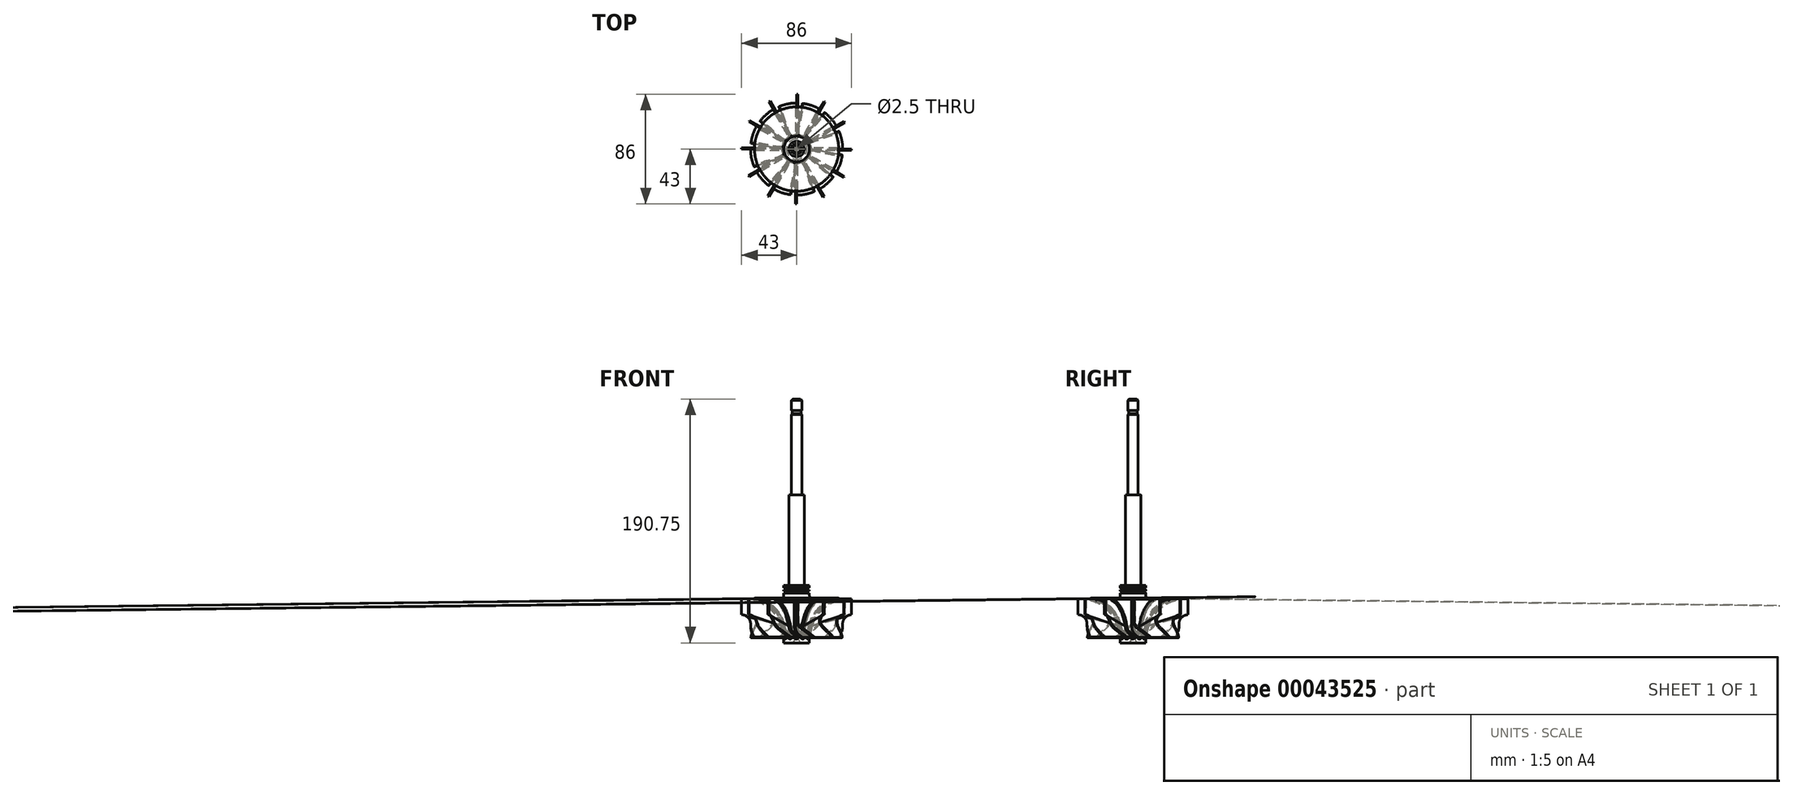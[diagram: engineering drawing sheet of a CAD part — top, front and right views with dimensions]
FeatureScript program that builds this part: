
annotation { "Feature Type Name" : "Feature", "Feature Type Description" : "" }
export const myFeature = defineFeature(function(context is Context, id is Id, definition is map)
    precondition{}
    {
        {
            var Q0;
            Q0=qCreatedBy(makeId("Front.planeOp"),FACE);
            var sketch = newSketch(context, id + "F0", { "sketchPlane" : qUnion([Q0])});
            skLineSegment(sketch, "E0", {"start": v(-6, -75) * mm, "end": v(-6, -145.75) * mm});
            skLineSegment(sketch, "E1", {"start": v(-43, -155.75) * mm, "end": v(-43, -168.75) * mm, "construction": true});
            skLineSegment(sketch, "E2", {"start": v(-43, -155.75) * mm, "end": v(-32.5, -155.75) * mm, "construction": true});
            skLineSegment(sketch, "E3", {"start": v(-10, -145.75) * mm, "end": v(-6, -145.75) * mm});
            skLineSegment(sketch, "E4", {"start": v(-6, -75) * mm, "end": v(-4, -75) * mm});
            skLineSegment(sketch, "E5", {"start": v(-4, 0) * mm, "end": v(0, 0) * mm});
            skLineSegment(sketch, "E6", {"start": v(0, 0) * mm, "end": v(0, -190.75) * mm});
            skLineSegment(sketch, "E7", {"start": v(-4, 0) * mm, "end": v(-4, -9) * mm});
            skLineSegment(sketch, "E8", {"start": v(-3.4, -9) * mm, "end": v(-3.4, -11.4) * mm});
            skLineSegment(sketch, "E9", {"start": v(-3.4, -11.4) * mm, "end": v(-4, -12) * mm});
            skLineSegment(sketch, "E10", {"start": v(-4, -12) * mm, "end": v(-4, -75) * mm});
            skLineSegment(sketch, "E11", {"start": v(-4, -9) * mm, "end": v(-3.4, -9) * mm});
            skLineSegment(sketch, "E12", {"start": v(-10, -145.75) * mm, "end": v(-10, -147.75) * mm});
            skLineSegment(sketch, "E13", {"start": v(-36, -175.75) * mm, "end": v(-36, -186.75) * mm, "construction": true});
            skLineSegment(sketch, "E14", {"start": v(-43, -168.75) * mm, "end": v(-43, -168.75) * mm});
            skLineSegment(sketch, "E15", {"start": v(-36, -186.75) * mm, "end": v(-10, -186.75) * mm, "construction": true});
            skLineSegment(sketch, "E16", {"start": v(-10, -186.75) * mm, "end": v(-10, -190.75) * mm});
            skLineSegment(sketch, "E17", {"start": v(-10, -190.75) * mm, "end": v(0, -190.75) * mm});
            skPoint(sketch, "E18.visualSharp", {"position": v(-36, -168.75) * mm});
            skArc(sketch, "E18.filletArc", {"start": v(-36, -175.75) * mm, "mid": v(-38.05, -170.8) * mm, "end": v(-43, -168.75) * mm, "construction": true});
            skLineSegment(sketch, "E19", {"start": v(-32.5, -155.75) * mm, "end": v(-32.5, -156.75) * mm, "construction": true});
            skArc(sketch, "E20", {"start": v(-32.5, -155.75) * mm, "mid": v(-33, -156.25) * mm, "end": v(-32.5, -156.75) * mm});
            skArc(sketch, "E21", {"start": v(-10, -186.75) * mm, "mid": v(-16.25, -168) * mm, "end": v(-32.5, -156.75) * mm});
            skLineSegment(sketch, "E22", {"start": v(-32.5, -155.75) * mm, "end": v(-10, -155.75) * mm});
            skLineSegment(sketch, "E23", {"start": v(-2.9, -190.75) * mm, "end": v(-1.5, -188.32) * mm});
            skLineSegment(sketch, "E24", {"start": v(-1.5, -188.32) * mm, "end": v(-1.5, -186.8) * mm});
            skLineSegment(sketch, "E25", {"start": v(-1.5, -186.8) * mm, "end": v(0, -185.9) * mm});
            skLineSegment(sketch, "E26", {"start": v(-8, -147.75) * mm, "end": v(-8, -149.25) * mm});
            skLineSegment(sketch, "E27", {"start": v(-8, -147.75) * mm, "end": v(-10, -147.75) * mm});
            skLineSegment(sketch, "E28", {"start": v(-8, -149.25) * mm, "end": v(-10, -149.25) * mm});
            skLineSegment(sketch, "E29", {"start": v(-8, -150.25) * mm, "end": v(-10, -150.25) * mm});
            skLineSegment(sketch, "E30", {"start": v(-8, -151.75) * mm, "end": v(-10, -151.75) * mm});
            skPoint(sketch, "E31.orphan", {"position": v(-8, -155.75) * mm});
            skLineSegment(sketch, "E32.trimOffspring", {"start": v(-8, -150.25) * mm, "end": v(-8, -151.75) * mm});
            skLineSegment(sketch, "E33.trimOffspring", {"start": v(-10, -149.25) * mm, "end": v(-10, -150.25) * mm});
            skLineSegment(sketch, "E34.trimOffspring", {"start": v(-10, -151.75) * mm, "end": v(-10, -155.75) * mm});
            skSolve(sketch);
        }
        {
            var Q0;
            Q0=qSketchRegion(id+"F0",true);
            var Q1;
            Q1=sQuery(id+"F0.wireOp",EDGE,"E6");
            revolve(context, id + "F1", {"entities" : qUnion([Q0]), "axis" : qUnion([Q1]), "revolveType" : RevolveType.FULL});
        }
        {
            var Q0;
            Q0=makeQuery(id+"F1.opRevolve","SWEPT_EDGE",EDGE,{"disambiguationData":[OSD([sQuery(id+"F0.wireOp",EDGE,"E22"),sQuery(id+"F0.wireOp",EDGE,"E34.trimOffspring")])]});
            fillet(context, id + "F2", {"entities" : qUnion([Q0]), "radius" : 2 * mm, "tangentPropagation" : true, "allowEdgeOverflow" : false});
        }
        {
            var Q0;
            Q0=makeQuery(id+"F1.opRevolve","SWEPT_EDGE",EDGE,{"disambiguationData":[OSD([sQuery(id+"F0.wireOp",EDGE,"E5"),sQuery(id+"F0.wireOp",EDGE,"E7")])]});
            chamfer(context, id + "F3", {"entities" : qUnion([Q0]), "width" : 1 * mm, "tangentPropagation" : true});
        }
        {
            var Q0;
            Q0=qCreatedBy(makeId("Front.planeOp"),FACE);
            var sketch = newSketch(context, id + "F4", { "sketchPlane" : qUnion([Q0])});
            skLineSegment(sketch, "E35", {"start": v(0, -1.47) * mm, "end": v(0, -247.78) * mm, "construction": true});
            skLineSegment(sketch, "E36", {"start": v(0, -155.75) * mm, "end": v(0, -181.26) * mm});
            skPoint(sketch, "E37.orphan", {"position": v(0.08, -187.45) * mm});
            skLineSegment(sketch, "E38", {"start": v(3, -186.75) * mm, "end": v(1.76, -185.5) * mm});
            skPoint(sketch, "E39.visualSharp", {"position": v(0, -183.75) * mm});
            skArc(sketch, "E39.filletArc", {"start": v(0, -181.26) * mm, "mid": v(0.46, -183.56) * mm, "end": v(1.76, -185.5) * mm});
            skLineSegment(sketch, "E40.0", {"start": v(1.59, -186.75) * mm, "end": v(1.05, -186.21) * mm});
            skArc(sketch, "E40.1", {"start": v(-1, -181.26) * mm, "mid": v(-0.47, -183.94) * mm, "end": v(1.05, -186.21) * mm});
            skLineSegment(sketch, "E40.2", {"start": v(-1, -155.75) * mm, "end": v(-1, -181.26) * mm});
            skLineSegment(sketch, "E41", {"start": v(-1, -155.75) * mm, "end": v(0, -155.75) * mm});
            skLineSegment(sketch, "E42", {"start": v(3, -186.75) * mm, "end": v(1.59, -186.75) * mm});
            skSolve(sketch);
        }
        {
            var Q0;
            Q0=qCreatedBy(makeId("Front.planeOp"),FACE);
            cPlane(context, id + "F5", {"entities" : qUnion([Q0]), "cplaneType" : CPlaneType.OFFSET, "offset" : 43 * mm, "width" : 150 * mm, "height" : 150 * mm});
        }
        {
            var Q0;
            Q0=qCreatedBy(id+"F5.planeOp",FACE);
            var sketch = newSketch(context, id + "F6", { "sketchPlane" : qUnion([Q0])});
            skLineSegment(sketch, "E43", {"start": v(0, -186.75) * mm, "end": v(18, -186.75) * mm, "construction": true});
            skLineSegment(sketch, "E44", {"start": v(0, -156.25) * mm, "end": v(0, -168.75) * mm});
            skLineSegment(sketch, "E45", {"start": v(18, -186.75) * mm, "end": v(4.42, -177.24) * mm});
            skArc(sketch, "E46", {"start": v(0, -168.75) * mm, "mid": v(1.17, -173.54) * mm, "end": v(4.42, -177.24) * mm});
            skLineSegment(sketch, "E47.0", {"start": v(16.26, -186.75) * mm, "end": v(3.85, -178.06) * mm});
            skArc(sketch, "E47.1", {"start": v(-1, -168.75) * mm, "mid": v(0.28, -174) * mm, "end": v(3.85, -178.06) * mm});
            skLineSegment(sketch, "E47.2", {"start": v(-1, -156.25) * mm, "end": v(-1, -168.75) * mm});
            skLineSegment(sketch, "E48", {"start": v(18, -186.75) * mm, "end": v(16.26, -186.75) * mm});
            skPoint(sketch, "E49.orphan", {"position": v(-14.5, -155.75) * mm});
            skPoint(sketch, "E50.orphan", {"position": v(14.5, -155.75) * mm});
            skLineSegment(sketch, "E51", {"start": v(0, -156.25) * mm, "end": v(-1, -156.25) * mm});
            skPoint(sketch, "E52.orphan", {"position": v(0, -155.75) * mm});
            skSolve(sketch);
        }
        {
            var Q1;
            Q1=qSketchRegion(id+"F4",true);
            var Q2;
            Q2=qSketchRegion(id+"F6",true);
            loft(context, id + "F7", {"operationType" : NewBodyOperationType.ADD, "sheetProfilesArray" : [{ "sheetProfileEntities" : qUnion([Q1]) }, { "sheetProfileEntities" : qUnion([Q2]) }]});
        }
        {
            var Q0;
            Q0=makeQuery(id+"F7.opLoft","SWEPT_FACE",FACE,{"disambiguationData":[OSD([sQuery(id+"F4.wireOp",EDGE,"E40.0"),sQuery(id+"F4.wireOp",EDGE,"E40.1"),sQuery(id+"F4.wireOp",EDGE,"E40.2"),sQuery(id+"F6.wireOp",EDGE,"E47.0"),sQuery(id+"F6.wireOp",EDGE,"E47.1"),sQuery(id+"F6.wireOp",EDGE,"E47.2")])]});
            var Q1;
            Q1=makeQuery(id+"F7.opLoft","SWEPT_FACE",FACE,{"disambiguationData":[OSD([sQuery(id+"F4.wireOp",EDGE,"E38"),sQuery(id+"F4.wireOp",EDGE,"E40.0"),sQuery(id+"F4.wireOp",EDGE,"E42"),sQuery(id+"F6.wireOp",EDGE,"E45"),sQuery(id+"F6.wireOp",EDGE,"E47.0"),sQuery(id+"F6.wireOp",EDGE,"E48")])]});
            var Q2;
            Q2=makeQuery(id+"F7.opLoft","CAP_FACE",FACE,{"disambiguationData":[OSD([makeQuery(id+"F6.imprint","IMPRINT",FACE,{"disambiguationData":[TD([[makeQuery(id+"F6.imprint","IMPRINT",EDGE,{"derivedFrom":sQuery(id+"F6.wireOp",EDGE,"E44")}),-1.0]])]})])],"isStart":true});
            var Q3;
            Q3=makeQuery(id+"F7.opLoft","SWEPT_FACE",FACE,{"disambiguationData":[OSD([sQuery(id+"F4.wireOp",EDGE,"E38"),sQuery(id+"F4.wireOp",EDGE,"E39.filletArc"),sQuery(id+"F4.wireOp",EDGE,"E42"),sQuery(id+"F6.wireOp",EDGE,"E45"),sQuery(id+"F6.wireOp",EDGE,"E46"),sQuery(id+"F6.wireOp",EDGE,"E48")])]});
            var Q4;
            Q4=makeQuery(id+"F7.opLoft","SWEPT_FACE",FACE,{"disambiguationData":[OSD([sQuery(id+"F4.wireOp",EDGE,"E36"),sQuery(id+"F4.wireOp",EDGE,"E39.filletArc"),sQuery(id+"F4.wireOp",EDGE,"E41"),sQuery(id+"F6.wireOp",EDGE,"E44"),sQuery(id+"F6.wireOp",EDGE,"E46"),sQuery(id+"F6.wireOp",EDGE,"E51")])]});
            var Q5;
            Q5=makeQuery(id+"F7.opLoft","SWEPT_FACE",FACE,{"disambiguationData":[OSD([sQuery(id+"F4.wireOp",EDGE,"E40.1"),sQuery(id+"F4.wireOp",EDGE,"E40.2"),sQuery(id+"F4.wireOp",EDGE,"E41"),sQuery(id+"F6.wireOp",EDGE,"E47.1"),sQuery(id+"F6.wireOp",EDGE,"E47.2"),sQuery(id+"F6.wireOp",EDGE,"E51")])]});
            var Q6;
            Q6=makeQuery(id+"F7.opLoft","SWEPT_FACE",FACE,{"disambiguationData":[OSD([sQuery(id+"F4.wireOp",EDGE,"E36"),sQuery(id+"F4.wireOp",EDGE,"E40.2"),sQuery(id+"F4.wireOp",EDGE,"E41"),sQuery(id+"F6.wireOp",EDGE,"E44"),sQuery(id+"F6.wireOp",EDGE,"E47.2"),sQuery(id+"F6.wireOp",EDGE,"E51")])]});
            var Q7;
            Q7=makeQuery(id+"F1.opRevolve","SWEPT_FACE",FACE,{"disambiguationData":[OSD([sQuery(id+"F0.wireOp",EDGE,"E0")])]});
            circularPattern(context, id + "F8", {"faces" : qUnion([Q0, Q1, Q2, Q3, Q4, Q5, Q6]), "axis" : qUnion([Q7]), "angle" : 30 * degree, "instanceCount" : round(12), "patternType" : PatternType.FACE});
        }
        {
            var Q0;
            Q0=qCreatedBy(makeId("Front.planeOp"),FACE);
            var sketch = newSketch(context, id + "F9", { "sketchPlane" : qUnion([Q0])});
            skLineSegment(sketch, "E53.0", {"start": v(43, -156.25) * mm, "end": v(43, -168.75) * mm});
            skLineSegment(sketch, "E54", {"start": v(43, -168.75) * mm, "end": v(43, -168.75) * mm});
            skLineSegment(sketch, "E55", {"start": v(36, -175.75) * mm, "end": v(36, -190.75) * mm});
            skLineSegment(sketch, "E56", {"start": v(0, 28.12) * mm, "end": v(0, -228.95) * mm, "construction": true});
            skLineSegment(sketch, "E57", {"start": v(43, -168.75) * mm, "end": v(50.1, -168.75) * mm});
            skLineSegment(sketch, "E58.0", {"start": v(-10, -190.75) * mm, "end": v(10, -190.75) * mm});
            skLineSegment(sketch, "E59", {"start": v(36, -190.75) * mm, "end": v(50.1, -190.75) * mm});
            skLineSegment(sketch, "E60", {"start": v(50.1, -168.75) * mm, "end": v(50.1, -190.75) * mm});
            skPoint(sketch, "E61.visualSharp", {"position": v(36, -168.75) * mm});
            skArc(sketch, "E61.filletArc", {"start": v(43, -168.75) * mm, "mid": v(38.05, -170.8) * mm, "end": v(36, -175.75) * mm});
            skSolve(sketch);
        }
        {
            var Q0;
            Q0=qSketchRegion(id+"F9",true);
            var Q1;
            Q1=sQuery(id+"F9.wireOp",EDGE,"E56");
            revolve(context, id + "F10", {"operationType" : NewBodyOperationType.REMOVE, "entities" : qUnion([Q0]), "axis" : qUnion([Q1]), "revolveType" : RevolveType.FULL, "oppositeDirection" : true});
        }
        {
            var Q0;
            Q0=qCreatedBy(makeId("Front.planeOp"),FACE);
            var sketch = newSketch(context, id + "F11", { "sketchPlane" : qUnion([Q0])});
            skLineSegment(sketch, "E62", {"start": v(0, 44.53) * mm, "end": v(0, -214.06) * mm, "construction": true});
            skLineSegment(sketch, "E63.0", {"start": v(0, -190.75) * mm, "end": v(2.98, -190.75) * mm});
            skLineSegment(sketch, "E64", {"start": v(0, -190.75) * mm, "end": v(0, -185) * mm});
            skLineSegment(sketch, "E65", {"start": v(0, -185) * mm, "end": v(1.25, -185.75) * mm});
            skLineSegment(sketch, "E66", {"start": v(1.25, -185.75) * mm, "end": v(1.25, -187.75) * mm});
            skLineSegment(sketch, "E67", {"start": v(1.25, -187.75) * mm, "end": v(2.98, -190.75) * mm});
            skPoint(sketch, "E68.orphan", {"position": v(10, -190.75) * mm});
            skPoint(sketch, "E69.orphan", {"position": v(-10, -190.75) * mm});
            skSolve(sketch);
        }
        {
            var Q0;
            Q0=qSketchRegion(id+"F11",true);
            var Q1;
            Q1=sQuery(id+"F11.wireOp",EDGE,"E62");
            revolve(context, id + "F12", {"operationType" : NewBodyOperationType.REMOVE, "entities" : qUnion([Q0]), "axis" : qUnion([Q1]), "revolveType" : RevolveType.FULL, "oppositeDirection" : true});
        }
        {
            var Q0;
            Q0=makeQuery(id+"F8.opPattern","COPY",EDGE,{"derivedFrom":makeQuery(id+"F7.opLoft","SWEPT_EDGE",EDGE,{"disambiguationData":[OSD([sQuery(id+"F4.wireOp",EDGE,"E38"),sQuery(id+"F4.wireOp",EDGE,"E42"),sQuery(id+"F6.wireOp",EDGE,"E45"),sQuery(id+"F6.wireOp",EDGE,"E48")])]}),"instanceName":"4"});
            var Q1;
            Q1=makeQuery(id+"F8.opPattern","COPY",EDGE,{"derivedFrom":makeQuery(id+"F7.opLoft","SWEPT_EDGE",EDGE,{"disambiguationData":[OSD([sQuery(id+"F4.wireOp",EDGE,"E38"),sQuery(id+"F4.wireOp",EDGE,"E42"),sQuery(id+"F6.wireOp",EDGE,"E45"),sQuery(id+"F6.wireOp",EDGE,"E48")])]}),"instanceName":"3"});
            var Q2;
            Q2=makeQuery(id+"F8.opPattern","COPY",EDGE,{"derivedFrom":makeQuery(id+"F7.opLoft","SWEPT_EDGE",EDGE,{"disambiguationData":[OSD([sQuery(id+"F4.wireOp",EDGE,"E38"),sQuery(id+"F4.wireOp",EDGE,"E42"),sQuery(id+"F6.wireOp",EDGE,"E45"),sQuery(id+"F6.wireOp",EDGE,"E48")])]}),"instanceName":"2"});
            var Q3;
            Q3=makeQuery(id+"F8.opPattern","COPY",EDGE,{"derivedFrom":makeQuery(id+"F7.opLoft","SWEPT_EDGE",EDGE,{"disambiguationData":[OSD([sQuery(id+"F4.wireOp",EDGE,"E38"),sQuery(id+"F4.wireOp",EDGE,"E42"),sQuery(id+"F6.wireOp",EDGE,"E45"),sQuery(id+"F6.wireOp",EDGE,"E48")])]}),"instanceName":"1"});
            var Q4;
            Q4=makeQuery(id+"F7.opLoft","SWEPT_EDGE",EDGE,{"disambiguationData":[OSD([sQuery(id+"F4.wireOp",EDGE,"E38"),sQuery(id+"F4.wireOp",EDGE,"E42"),sQuery(id+"F6.wireOp",EDGE,"E45"),sQuery(id+"F6.wireOp",EDGE,"E48")])]});
            var Q5;
            Q5=makeQuery(id+"F8.opPattern","COPY",EDGE,{"derivedFrom":makeQuery(id+"F7.opLoft","SWEPT_EDGE",EDGE,{"disambiguationData":[OSD([sQuery(id+"F4.wireOp",EDGE,"E38"),sQuery(id+"F4.wireOp",EDGE,"E42"),sQuery(id+"F6.wireOp",EDGE,"E45"),sQuery(id+"F6.wireOp",EDGE,"E48")])]}),"instanceName":"11"});
            var Q6;
            Q6=makeQuery(id+"F8.opPattern","COPY",EDGE,{"derivedFrom":makeQuery(id+"F7.opLoft","SWEPT_EDGE",EDGE,{"disambiguationData":[OSD([sQuery(id+"F4.wireOp",EDGE,"E38"),sQuery(id+"F4.wireOp",EDGE,"E42"),sQuery(id+"F6.wireOp",EDGE,"E45"),sQuery(id+"F6.wireOp",EDGE,"E48")])]}),"instanceName":"10"});
            var Q7;
            Q7=makeQuery(id+"F8.opPattern","COPY",EDGE,{"derivedFrom":makeQuery(id+"F7.opLoft","SWEPT_EDGE",EDGE,{"disambiguationData":[OSD([sQuery(id+"F4.wireOp",EDGE,"E38"),sQuery(id+"F4.wireOp",EDGE,"E42"),sQuery(id+"F6.wireOp",EDGE,"E45"),sQuery(id+"F6.wireOp",EDGE,"E48")])]}),"instanceName":"9"});
            var Q8;
            Q8=makeQuery(id+"F8.opPattern","COPY",EDGE,{"derivedFrom":makeQuery(id+"F7.opLoft","SWEPT_EDGE",EDGE,{"disambiguationData":[OSD([sQuery(id+"F4.wireOp",EDGE,"E38"),sQuery(id+"F4.wireOp",EDGE,"E42"),sQuery(id+"F6.wireOp",EDGE,"E45"),sQuery(id+"F6.wireOp",EDGE,"E48")])]}),"instanceName":"8"});
            var Q9;
            Q9=makeQuery(id+"F8.opPattern","COPY",EDGE,{"derivedFrom":makeQuery(id+"F7.opLoft","SWEPT_EDGE",EDGE,{"disambiguationData":[OSD([sQuery(id+"F4.wireOp",EDGE,"E38"),sQuery(id+"F4.wireOp",EDGE,"E42"),sQuery(id+"F6.wireOp",EDGE,"E45"),sQuery(id+"F6.wireOp",EDGE,"E48")])]}),"instanceName":"7"});
            var Q10;
            Q10=makeQuery(id+"F8.opPattern","COPY",EDGE,{"derivedFrom":makeQuery(id+"F7.opLoft","SWEPT_EDGE",EDGE,{"disambiguationData":[OSD([sQuery(id+"F4.wireOp",EDGE,"E38"),sQuery(id+"F4.wireOp",EDGE,"E42"),sQuery(id+"F6.wireOp",EDGE,"E45"),sQuery(id+"F6.wireOp",EDGE,"E48")])]}),"instanceName":"6"});
            var Q11;
            Q11=makeQuery(id+"F8.opPattern","COPY",EDGE,{"derivedFrom":makeQuery(id+"F7.opLoft","SWEPT_EDGE",EDGE,{"disambiguationData":[OSD([sQuery(id+"F4.wireOp",EDGE,"E38"),sQuery(id+"F4.wireOp",EDGE,"E42"),sQuery(id+"F6.wireOp",EDGE,"E45"),sQuery(id+"F6.wireOp",EDGE,"E48")])]}),"instanceName":"5"});
            fillet(context, id + "F13", {"entities" : qUnion([Q0, Q1, Q2, Q3, Q4, Q5, Q6, Q7, Q8, Q9, Q10, Q11]), "radius" : .3 * mm, "tangentPropagation" : true, "allowEdgeOverflow" : false});
        }
        {
            var Q0;
            Q0=makeQuery(id+"F8.opPattern","COPY",EDGE,{"derivedFrom":makeQuery(id+"F7.opLoft","SWEPT_EDGE",EDGE,{"disambiguationData":[OSD([sQuery(id+"F4.wireOp",EDGE,"E40.0"),sQuery(id+"F4.wireOp",EDGE,"E42"),sQuery(id+"F6.wireOp",EDGE,"E47.0"),sQuery(id+"F6.wireOp",EDGE,"E48")])]}),"instanceName":"5"});
            var Q1;
            Q1=makeQuery(id+"F8.opPattern","COPY",EDGE,{"derivedFrom":makeQuery(id+"F7.opLoft","SWEPT_EDGE",EDGE,{"disambiguationData":[OSD([sQuery(id+"F4.wireOp",EDGE,"E40.0"),sQuery(id+"F4.wireOp",EDGE,"E42"),sQuery(id+"F6.wireOp",EDGE,"E47.0"),sQuery(id+"F6.wireOp",EDGE,"E48")])]}),"instanceName":"4"});
            var Q2;
            Q2=makeQuery(id+"F8.opPattern","COPY",EDGE,{"derivedFrom":makeQuery(id+"F7.opLoft","SWEPT_EDGE",EDGE,{"disambiguationData":[OSD([sQuery(id+"F4.wireOp",EDGE,"E40.0"),sQuery(id+"F4.wireOp",EDGE,"E42"),sQuery(id+"F6.wireOp",EDGE,"E47.0"),sQuery(id+"F6.wireOp",EDGE,"E48")])]}),"instanceName":"3"});
            var Q3;
            Q3=makeQuery(id+"F8.opPattern","COPY",EDGE,{"derivedFrom":makeQuery(id+"F7.opLoft","SWEPT_EDGE",EDGE,{"disambiguationData":[OSD([sQuery(id+"F4.wireOp",EDGE,"E40.0"),sQuery(id+"F4.wireOp",EDGE,"E42"),sQuery(id+"F6.wireOp",EDGE,"E47.0"),sQuery(id+"F6.wireOp",EDGE,"E48")])]}),"instanceName":"2"});
            var Q4;
            Q4=makeQuery(id+"F8.opPattern","COPY",EDGE,{"derivedFrom":makeQuery(id+"F7.opLoft","SWEPT_EDGE",EDGE,{"disambiguationData":[OSD([sQuery(id+"F4.wireOp",EDGE,"E40.0"),sQuery(id+"F4.wireOp",EDGE,"E42"),sQuery(id+"F6.wireOp",EDGE,"E47.0"),sQuery(id+"F6.wireOp",EDGE,"E48")])]}),"instanceName":"1"});
            var Q5;
            Q5=makeQuery(id+"F7.opLoft","SWEPT_EDGE",EDGE,{"disambiguationData":[OSD([sQuery(id+"F4.wireOp",EDGE,"E40.0"),sQuery(id+"F4.wireOp",EDGE,"E42"),sQuery(id+"F6.wireOp",EDGE,"E47.0"),sQuery(id+"F6.wireOp",EDGE,"E48")])]});
            var Q6;
            Q6=makeQuery(id+"F8.opPattern","COPY",EDGE,{"derivedFrom":makeQuery(id+"F7.opLoft","SWEPT_EDGE",EDGE,{"disambiguationData":[OSD([sQuery(id+"F4.wireOp",EDGE,"E40.0"),sQuery(id+"F4.wireOp",EDGE,"E42"),sQuery(id+"F6.wireOp",EDGE,"E47.0"),sQuery(id+"F6.wireOp",EDGE,"E48")])]}),"instanceName":"11"});
            var Q7;
            Q7=makeQuery(id+"F8.opPattern","COPY",EDGE,{"derivedFrom":makeQuery(id+"F7.opLoft","SWEPT_EDGE",EDGE,{"disambiguationData":[OSD([sQuery(id+"F4.wireOp",EDGE,"E40.0"),sQuery(id+"F4.wireOp",EDGE,"E42"),sQuery(id+"F6.wireOp",EDGE,"E47.0"),sQuery(id+"F6.wireOp",EDGE,"E48")])]}),"instanceName":"10"});
            var Q8;
            Q8=makeQuery(id+"F8.opPattern","COPY",EDGE,{"derivedFrom":makeQuery(id+"F7.opLoft","SWEPT_EDGE",EDGE,{"disambiguationData":[OSD([sQuery(id+"F4.wireOp",EDGE,"E40.0"),sQuery(id+"F4.wireOp",EDGE,"E42"),sQuery(id+"F6.wireOp",EDGE,"E47.0"),sQuery(id+"F6.wireOp",EDGE,"E48")])]}),"instanceName":"9"});
            var Q9;
            Q9=makeQuery(id+"F8.opPattern","COPY",EDGE,{"derivedFrom":makeQuery(id+"F7.opLoft","SWEPT_EDGE",EDGE,{"disambiguationData":[OSD([sQuery(id+"F4.wireOp",EDGE,"E40.0"),sQuery(id+"F4.wireOp",EDGE,"E42"),sQuery(id+"F6.wireOp",EDGE,"E47.0"),sQuery(id+"F6.wireOp",EDGE,"E48")])]}),"instanceName":"8"});
            var Q10;
            Q10=makeQuery(id+"F8.opPattern","COPY",EDGE,{"derivedFrom":makeQuery(id+"F7.opLoft","SWEPT_EDGE",EDGE,{"disambiguationData":[OSD([sQuery(id+"F4.wireOp",EDGE,"E40.0"),sQuery(id+"F4.wireOp",EDGE,"E42"),sQuery(id+"F6.wireOp",EDGE,"E47.0"),sQuery(id+"F6.wireOp",EDGE,"E48")])]}),"instanceName":"7"});
            var Q11;
            Q11=makeQuery(id+"F8.opPattern","COPY",EDGE,{"derivedFrom":makeQuery(id+"F7.opLoft","SWEPT_EDGE",EDGE,{"disambiguationData":[OSD([sQuery(id+"F4.wireOp",EDGE,"E40.0"),sQuery(id+"F4.wireOp",EDGE,"E42"),sQuery(id+"F6.wireOp",EDGE,"E47.0"),sQuery(id+"F6.wireOp",EDGE,"E48")])]}),"instanceName":"6"});
            fillet(context, id + "F14", {"entities" : qUnion([Q0, Q1, Q2, Q3, Q4, Q5, Q6, Q7, Q8, Q9, Q10, Q11]), "radius" : 1.5 * mm, "tangentPropagation" : true, "allowEdgeOverflow" : false});
        }
        {
            var Q0;
            Q0=makeQuery(id+"F8.opPattern","COPY",EDGE,{"derivedFrom":makeQuery(id+"F7.boolean.opBoolean","INTERSECT",EDGE,{"derivedFrom":[makeQuery(id+"F1.opRevolve","SWEPT_FACE",FACE,{"disambiguationData":[OSD([sQuery(id+"F0.wireOp",EDGE,"E21")])]}),makeQuery(id+"F7.opLoft","SWEPT_FACE",FACE,{"disambiguationData":[OSD([sQuery(id+"F4.wireOp",EDGE,"E36"),sQuery(id+"F4.wireOp",EDGE,"E39.filletArc"),sQuery(id+"F4.wireOp",EDGE,"E41"),sQuery(id+"F6.wireOp",EDGE,"E44"),sQuery(id+"F6.wireOp",EDGE,"E46"),sQuery(id+"F6.wireOp",EDGE,"E51")])]})]}),"instanceName":"5"});
            var Q1;
            Q1=makeQuery(id+"F8.opPattern","COPY",EDGE,{"derivedFrom":makeQuery(id+"F7.boolean.opBoolean","INTERSECT",EDGE,{"derivedFrom":[makeQuery(id+"F1.opRevolve","SWEPT_FACE",FACE,{"disambiguationData":[OSD([sQuery(id+"F0.wireOp",EDGE,"E21")])]}),makeQuery(id+"F7.opLoft","SWEPT_FACE",FACE,{"disambiguationData":[OSD([sQuery(id+"F4.wireOp",EDGE,"E38"),sQuery(id+"F4.wireOp",EDGE,"E39.filletArc"),sQuery(id+"F4.wireOp",EDGE,"E42"),sQuery(id+"F6.wireOp",EDGE,"E45"),sQuery(id+"F6.wireOp",EDGE,"E46"),sQuery(id+"F6.wireOp",EDGE,"E48")])]})]}),"instanceName":"5"});
            var Q2;
            Q2=makeQuery(id+"F13.opFillet","BLEND_EDGE",EDGE,{"blendedFrom":[makeQuery(id+"F8.opPattern","COPY",EDGE,{"derivedFrom":makeQuery(id+"F7.opLoft","SWEPT_EDGE",EDGE,{"disambiguationData":[OSD([sQuery(id+"F4.wireOp",EDGE,"E38"),sQuery(id+"F4.wireOp",EDGE,"E42"),sQuery(id+"F6.wireOp",EDGE,"E45"),sQuery(id+"F6.wireOp",EDGE,"E48")])]}),"instanceName":"5"}),makeQuery(id+"F8.opPattern","SPLIT",FACE,{"disambiguationData":[OD(6.0)],"derivedFrom":makeQuery(id+"F1.opRevolve","SWEPT_FACE",FACE,{"disambiguationData":[OSD([sQuery(id+"F0.wireOp",EDGE,"E21")])]})})],"blendedInto":[makeQuery(id+"F8.opPattern","SPLIT",FACE,{"disambiguationData":[OD(6.0)],"derivedFrom":makeQuery(id+"F1.opRevolve","SWEPT_FACE",FACE,{"disambiguationData":[OSD([sQuery(id+"F0.wireOp",EDGE,"E21")])]})})]});
            var Q3;
            Q3=makeQuery(id+"F8.opPattern","COPY",EDGE,{"derivedFrom":makeQuery(id+"F7.boolean.opBoolean","SPLIT",EDGE,{"disambiguationData":[OD(1.0)],"derivedFrom":makeQuery(id+"F1.opRevolve","SWEPT_EDGE",EDGE,{"disambiguationData":[OSD([sQuery(id+"F0.wireOp",EDGE,"E16"),sQuery(id+"F0.wireOp",EDGE,"E21")])]})}),"instanceName":"5"});
            var Q4;
            Q4=makeQuery(id+"F14.opFillet","BLEND_EDGE",EDGE,{"blendedFrom":[makeQuery(id+"F8.opPattern","COPY",EDGE,{"derivedFrom":makeQuery(id+"F7.opLoft","SWEPT_EDGE",EDGE,{"disambiguationData":[OSD([sQuery(id+"F4.wireOp",EDGE,"E40.0"),sQuery(id+"F4.wireOp",EDGE,"E42"),sQuery(id+"F6.wireOp",EDGE,"E47.0"),sQuery(id+"F6.wireOp",EDGE,"E48")])]}),"instanceName":"5"}),makeQuery(id+"F8.opPattern","SPLIT",FACE,{"disambiguationData":[OD(5.0)],"derivedFrom":makeQuery(id+"F1.opRevolve","SWEPT_FACE",FACE,{"disambiguationData":[OSD([sQuery(id+"F0.wireOp",EDGE,"E21")])]})})],"blendedInto":[makeQuery(id+"F8.opPattern","SPLIT",FACE,{"disambiguationData":[OD(5.0)],"derivedFrom":makeQuery(id+"F1.opRevolve","SWEPT_FACE",FACE,{"disambiguationData":[OSD([sQuery(id+"F0.wireOp",EDGE,"E21")])]})})]});
            var Q5;
            Q5=makeQuery(id+"F8.opPattern","COPY",EDGE,{"derivedFrom":makeQuery(id+"F7.boolean.opBoolean","INTERSECT",EDGE,{"derivedFrom":[makeQuery(id+"F1.opRevolve","SWEPT_FACE",FACE,{"disambiguationData":[OSD([sQuery(id+"F0.wireOp",EDGE,"E21")])]}),makeQuery(id+"F7.opLoft","SWEPT_FACE",FACE,{"disambiguationData":[OSD([sQuery(id+"F4.wireOp",EDGE,"E40.0"),sQuery(id+"F4.wireOp",EDGE,"E40.1"),sQuery(id+"F4.wireOp",EDGE,"E40.2"),sQuery(id+"F6.wireOp",EDGE,"E47.0"),sQuery(id+"F6.wireOp",EDGE,"E47.1"),sQuery(id+"F6.wireOp",EDGE,"E47.2")])]})]}),"instanceName":"5"});
            var Q6;
            Q6=makeQuery(id+"F8.opPattern","COPY",EDGE,{"derivedFrom":makeQuery(id+"F7.boolean.opBoolean","INTERSECT",EDGE,{"derivedFrom":[makeQuery(id+"F1.opRevolve","SWEPT_FACE",FACE,{"disambiguationData":[OSD([sQuery(id+"F0.wireOp",EDGE,"E21")])]}),makeQuery(id+"F7.opLoft","SWEPT_FACE",FACE,{"disambiguationData":[OSD([sQuery(id+"F4.wireOp",EDGE,"E40.1"),sQuery(id+"F4.wireOp",EDGE,"E40.2"),sQuery(id+"F4.wireOp",EDGE,"E41"),sQuery(id+"F6.wireOp",EDGE,"E47.1"),sQuery(id+"F6.wireOp",EDGE,"E47.2"),sQuery(id+"F6.wireOp",EDGE,"E51")])]})]}),"instanceName":"5"});
            var Q7;
            Q7=makeQuery(id+"F8.opPattern","COPY",EDGE,{"derivedFrom":makeQuery(id+"F7.boolean.opBoolean","INTERSECT",EDGE,{"derivedFrom":[makeQuery(id+"F1.opRevolve","SWEPT_FACE",FACE,{"disambiguationData":[OSD([sQuery(id+"F0.wireOp",EDGE,"E20")])]}),makeQuery(id+"F7.opLoft","SWEPT_FACE",FACE,{"disambiguationData":[OSD([sQuery(id+"F4.wireOp",EDGE,"E40.1"),sQuery(id+"F4.wireOp",EDGE,"E40.2"),sQuery(id+"F4.wireOp",EDGE,"E41"),sQuery(id+"F6.wireOp",EDGE,"E47.1"),sQuery(id+"F6.wireOp",EDGE,"E47.2"),sQuery(id+"F6.wireOp",EDGE,"E51")])]})]}),"instanceName":"5"});
            var Q8;
            Q8=makeQuery(id+"F8.opPattern","COPY",EDGE,{"derivedFrom":makeQuery(id+"F7.boolean.opBoolean","INTERSECT",EDGE,{"derivedFrom":[makeQuery(id+"F1.opRevolve","SWEPT_FACE",FACE,{"disambiguationData":[OSD([sQuery(id+"F0.wireOp",EDGE,"E20")])]}),makeQuery(id+"F7.opLoft","SWEPT_FACE",FACE,{"disambiguationData":[OSD([sQuery(id+"F4.wireOp",EDGE,"E36"),sQuery(id+"F4.wireOp",EDGE,"E39.filletArc"),sQuery(id+"F4.wireOp",EDGE,"E41"),sQuery(id+"F6.wireOp",EDGE,"E44"),sQuery(id+"F6.wireOp",EDGE,"E46"),sQuery(id+"F6.wireOp",EDGE,"E51")])]})]}),"instanceName":"5"});
            var Q9;
            Q9=makeQuery(id+"F8.opPattern","COPY",EDGE,{"derivedFrom":makeQuery(id+"F7.boolean.opBoolean","INTERSECT",EDGE,{"derivedFrom":[makeQuery(id+"F1.opRevolve","SWEPT_FACE",FACE,{"disambiguationData":[OSD([sQuery(id+"F0.wireOp",EDGE,"E20")])]}),makeQuery(id+"F7.opLoft","SWEPT_FACE",FACE,{"disambiguationData":[OSD([sQuery(id+"F4.wireOp",EDGE,"E36"),sQuery(id+"F4.wireOp",EDGE,"E40.2"),sQuery(id+"F4.wireOp",EDGE,"E41"),sQuery(id+"F6.wireOp",EDGE,"E44"),sQuery(id+"F6.wireOp",EDGE,"E47.2"),sQuery(id+"F6.wireOp",EDGE,"E51")])]})]}),"instanceName":"5"});
            var Q10;
            Q10=makeQuery(id+"F8.opPattern","COPY",EDGE,{"derivedFrom":makeQuery(id+"F7.boolean.opBoolean","INTERSECT",EDGE,{"derivedFrom":[makeQuery(id+"F1.opRevolve","SWEPT_FACE",FACE,{"disambiguationData":[OSD([sQuery(id+"F0.wireOp",EDGE,"E21")])]}),makeQuery(id+"F7.opLoft","SWEPT_FACE",FACE,{"disambiguationData":[OSD([sQuery(id+"F4.wireOp",EDGE,"E36"),sQuery(id+"F4.wireOp",EDGE,"E39.filletArc"),sQuery(id+"F4.wireOp",EDGE,"E41"),sQuery(id+"F6.wireOp",EDGE,"E44"),sQuery(id+"F6.wireOp",EDGE,"E46"),sQuery(id+"F6.wireOp",EDGE,"E51")])]})]}),"instanceName":"6"});
            var Q11;
            Q11=makeQuery(id+"F8.opPattern","COPY",EDGE,{"derivedFrom":makeQuery(id+"F7.boolean.opBoolean","INTERSECT",EDGE,{"derivedFrom":[makeQuery(id+"F1.opRevolve","SWEPT_FACE",FACE,{"disambiguationData":[OSD([sQuery(id+"F0.wireOp",EDGE,"E21")])]}),makeQuery(id+"F7.opLoft","SWEPT_FACE",FACE,{"disambiguationData":[OSD([sQuery(id+"F4.wireOp",EDGE,"E38"),sQuery(id+"F4.wireOp",EDGE,"E39.filletArc"),sQuery(id+"F4.wireOp",EDGE,"E42"),sQuery(id+"F6.wireOp",EDGE,"E45"),sQuery(id+"F6.wireOp",EDGE,"E46"),sQuery(id+"F6.wireOp",EDGE,"E48")])]})]}),"instanceName":"6"});
            var Q12;
            Q12=makeQuery(id+"F13.opFillet","BLEND_EDGE",EDGE,{"blendedFrom":[makeQuery(id+"F8.opPattern","COPY",EDGE,{"derivedFrom":makeQuery(id+"F7.opLoft","SWEPT_EDGE",EDGE,{"disambiguationData":[OSD([sQuery(id+"F4.wireOp",EDGE,"E38"),sQuery(id+"F4.wireOp",EDGE,"E42"),sQuery(id+"F6.wireOp",EDGE,"E45"),sQuery(id+"F6.wireOp",EDGE,"E48")])]}),"instanceName":"6"}),makeQuery(id+"F8.opPattern","SPLIT",FACE,{"disambiguationData":[OD(7.0)],"derivedFrom":makeQuery(id+"F1.opRevolve","SWEPT_FACE",FACE,{"disambiguationData":[OSD([sQuery(id+"F0.wireOp",EDGE,"E21")])]})})],"blendedInto":[makeQuery(id+"F8.opPattern","SPLIT",FACE,{"disambiguationData":[OD(7.0)],"derivedFrom":makeQuery(id+"F1.opRevolve","SWEPT_FACE",FACE,{"disambiguationData":[OSD([sQuery(id+"F0.wireOp",EDGE,"E21")])]})})]});
            var Q13;
            Q13=makeQuery(id+"F8.opPattern","COPY",EDGE,{"derivedFrom":makeQuery(id+"F7.boolean.opBoolean","SPLIT",EDGE,{"disambiguationData":[OD(1.0)],"derivedFrom":makeQuery(id+"F1.opRevolve","SWEPT_EDGE",EDGE,{"disambiguationData":[OSD([sQuery(id+"F0.wireOp",EDGE,"E16"),sQuery(id+"F0.wireOp",EDGE,"E21")])]})}),"instanceName":"6"});
            var Q14;
            Q14=makeQuery(id+"F14.opFillet","BLEND_EDGE",EDGE,{"blendedFrom":[makeQuery(id+"F8.opPattern","COPY",EDGE,{"derivedFrom":makeQuery(id+"F7.opLoft","SWEPT_EDGE",EDGE,{"disambiguationData":[OSD([sQuery(id+"F4.wireOp",EDGE,"E40.0"),sQuery(id+"F4.wireOp",EDGE,"E42"),sQuery(id+"F6.wireOp",EDGE,"E47.0"),sQuery(id+"F6.wireOp",EDGE,"E48")])]}),"instanceName":"6"}),makeQuery(id+"F8.opPattern","SPLIT",FACE,{"disambiguationData":[OD(6.0)],"derivedFrom":makeQuery(id+"F1.opRevolve","SWEPT_FACE",FACE,{"disambiguationData":[OSD([sQuery(id+"F0.wireOp",EDGE,"E21")])]})})],"blendedInto":[makeQuery(id+"F8.opPattern","SPLIT",FACE,{"disambiguationData":[OD(6.0)],"derivedFrom":makeQuery(id+"F1.opRevolve","SWEPT_FACE",FACE,{"disambiguationData":[OSD([sQuery(id+"F0.wireOp",EDGE,"E21")])]})})]});
            var Q15;
            Q15=makeQuery(id+"F8.opPattern","COPY",EDGE,{"derivedFrom":makeQuery(id+"F7.boolean.opBoolean","INTERSECT",EDGE,{"derivedFrom":[makeQuery(id+"F1.opRevolve","SWEPT_FACE",FACE,{"disambiguationData":[OSD([sQuery(id+"F0.wireOp",EDGE,"E21")])]}),makeQuery(id+"F7.opLoft","SWEPT_FACE",FACE,{"disambiguationData":[OSD([sQuery(id+"F4.wireOp",EDGE,"E40.0"),sQuery(id+"F4.wireOp",EDGE,"E40.1"),sQuery(id+"F4.wireOp",EDGE,"E40.2"),sQuery(id+"F6.wireOp",EDGE,"E47.0"),sQuery(id+"F6.wireOp",EDGE,"E47.1"),sQuery(id+"F6.wireOp",EDGE,"E47.2")])]})]}),"instanceName":"6"});
            var Q16;
            Q16=makeQuery(id+"F8.opPattern","COPY",EDGE,{"derivedFrom":makeQuery(id+"F7.boolean.opBoolean","INTERSECT",EDGE,{"derivedFrom":[makeQuery(id+"F1.opRevolve","SWEPT_FACE",FACE,{"disambiguationData":[OSD([sQuery(id+"F0.wireOp",EDGE,"E21")])]}),makeQuery(id+"F7.opLoft","SWEPT_FACE",FACE,{"disambiguationData":[OSD([sQuery(id+"F4.wireOp",EDGE,"E40.1"),sQuery(id+"F4.wireOp",EDGE,"E40.2"),sQuery(id+"F4.wireOp",EDGE,"E41"),sQuery(id+"F6.wireOp",EDGE,"E47.1"),sQuery(id+"F6.wireOp",EDGE,"E47.2"),sQuery(id+"F6.wireOp",EDGE,"E51")])]})]}),"instanceName":"6"});
            var Q17;
            Q17=makeQuery(id+"F8.opPattern","COPY",EDGE,{"derivedFrom":makeQuery(id+"F7.boolean.opBoolean","INTERSECT",EDGE,{"derivedFrom":[makeQuery(id+"F1.opRevolve","SWEPT_FACE",FACE,{"disambiguationData":[OSD([sQuery(id+"F0.wireOp",EDGE,"E20")])]}),makeQuery(id+"F7.opLoft","SWEPT_FACE",FACE,{"disambiguationData":[OSD([sQuery(id+"F4.wireOp",EDGE,"E40.1"),sQuery(id+"F4.wireOp",EDGE,"E40.2"),sQuery(id+"F4.wireOp",EDGE,"E41"),sQuery(id+"F6.wireOp",EDGE,"E47.1"),sQuery(id+"F6.wireOp",EDGE,"E47.2"),sQuery(id+"F6.wireOp",EDGE,"E51")])]})]}),"instanceName":"6"});
            var Q18;
            Q18=makeQuery(id+"F8.opPattern","COPY",EDGE,{"derivedFrom":makeQuery(id+"F7.boolean.opBoolean","INTERSECT",EDGE,{"derivedFrom":[makeQuery(id+"F1.opRevolve","SWEPT_FACE",FACE,{"disambiguationData":[OSD([sQuery(id+"F0.wireOp",EDGE,"E20")])]}),makeQuery(id+"F7.opLoft","SWEPT_FACE",FACE,{"disambiguationData":[OSD([sQuery(id+"F4.wireOp",EDGE,"E36"),sQuery(id+"F4.wireOp",EDGE,"E39.filletArc"),sQuery(id+"F4.wireOp",EDGE,"E41"),sQuery(id+"F6.wireOp",EDGE,"E44"),sQuery(id+"F6.wireOp",EDGE,"E46"),sQuery(id+"F6.wireOp",EDGE,"E51")])]})]}),"instanceName":"6"});
            var Q19;
            Q19=makeQuery(id+"F8.opPattern","COPY",EDGE,{"derivedFrom":makeQuery(id+"F7.boolean.opBoolean","INTERSECT",EDGE,{"derivedFrom":[makeQuery(id+"F1.opRevolve","SWEPT_FACE",FACE,{"disambiguationData":[OSD([sQuery(id+"F0.wireOp",EDGE,"E20")])]}),makeQuery(id+"F7.opLoft","SWEPT_FACE",FACE,{"disambiguationData":[OSD([sQuery(id+"F4.wireOp",EDGE,"E36"),sQuery(id+"F4.wireOp",EDGE,"E40.2"),sQuery(id+"F4.wireOp",EDGE,"E41"),sQuery(id+"F6.wireOp",EDGE,"E44"),sQuery(id+"F6.wireOp",EDGE,"E47.2"),sQuery(id+"F6.wireOp",EDGE,"E51")])]})]}),"instanceName":"6"});
            var Q20;
            Q20=makeQuery(id+"F8.opPattern","COPY",EDGE,{"derivedFrom":makeQuery(id+"F7.boolean.opBoolean","INTERSECT",EDGE,{"derivedFrom":[makeQuery(id+"F1.opRevolve","SWEPT_FACE",FACE,{"disambiguationData":[OSD([sQuery(id+"F0.wireOp",EDGE,"E21")])]}),makeQuery(id+"F7.opLoft","SWEPT_FACE",FACE,{"disambiguationData":[OSD([sQuery(id+"F4.wireOp",EDGE,"E36"),sQuery(id+"F4.wireOp",EDGE,"E39.filletArc"),sQuery(id+"F4.wireOp",EDGE,"E41"),sQuery(id+"F6.wireOp",EDGE,"E44"),sQuery(id+"F6.wireOp",EDGE,"E46"),sQuery(id+"F6.wireOp",EDGE,"E51")])]})]}),"instanceName":"7"});
            var Q21;
            Q21=makeQuery(id+"F8.opPattern","COPY",EDGE,{"derivedFrom":makeQuery(id+"F7.boolean.opBoolean","INTERSECT",EDGE,{"derivedFrom":[makeQuery(id+"F1.opRevolve","SWEPT_FACE",FACE,{"disambiguationData":[OSD([sQuery(id+"F0.wireOp",EDGE,"E21")])]}),makeQuery(id+"F7.opLoft","SWEPT_FACE",FACE,{"disambiguationData":[OSD([sQuery(id+"F4.wireOp",EDGE,"E38"),sQuery(id+"F4.wireOp",EDGE,"E39.filletArc"),sQuery(id+"F4.wireOp",EDGE,"E42"),sQuery(id+"F6.wireOp",EDGE,"E45"),sQuery(id+"F6.wireOp",EDGE,"E46"),sQuery(id+"F6.wireOp",EDGE,"E48")])]})]}),"instanceName":"7"});
            var Q22;
            Q22=makeQuery(id+"F13.opFillet","BLEND_EDGE",EDGE,{"blendedFrom":[makeQuery(id+"F8.opPattern","COPY",EDGE,{"derivedFrom":makeQuery(id+"F7.opLoft","SWEPT_EDGE",EDGE,{"disambiguationData":[OSD([sQuery(id+"F4.wireOp",EDGE,"E38"),sQuery(id+"F4.wireOp",EDGE,"E42"),sQuery(id+"F6.wireOp",EDGE,"E45"),sQuery(id+"F6.wireOp",EDGE,"E48")])]}),"instanceName":"7"}),makeQuery(id+"F8.opPattern","SPLIT",FACE,{"disambiguationData":[OD(8.0)],"derivedFrom":makeQuery(id+"F1.opRevolve","SWEPT_FACE",FACE,{"disambiguationData":[OSD([sQuery(id+"F0.wireOp",EDGE,"E21")])]})})],"blendedInto":[makeQuery(id+"F8.opPattern","SPLIT",FACE,{"disambiguationData":[OD(8.0)],"derivedFrom":makeQuery(id+"F1.opRevolve","SWEPT_FACE",FACE,{"disambiguationData":[OSD([sQuery(id+"F0.wireOp",EDGE,"E21")])]})})]});
            var Q23;
            Q23=makeQuery(id+"F8.opPattern","COPY",EDGE,{"derivedFrom":makeQuery(id+"F7.boolean.opBoolean","SPLIT",EDGE,{"disambiguationData":[OD(1.0)],"derivedFrom":makeQuery(id+"F1.opRevolve","SWEPT_EDGE",EDGE,{"disambiguationData":[OSD([sQuery(id+"F0.wireOp",EDGE,"E16"),sQuery(id+"F0.wireOp",EDGE,"E21")])]})}),"instanceName":"7"});
            var Q24;
            Q24=makeQuery(id+"F14.opFillet","BLEND_EDGE",EDGE,{"blendedFrom":[makeQuery(id+"F8.opPattern","COPY",EDGE,{"derivedFrom":makeQuery(id+"F7.opLoft","SWEPT_EDGE",EDGE,{"disambiguationData":[OSD([sQuery(id+"F4.wireOp",EDGE,"E40.0"),sQuery(id+"F4.wireOp",EDGE,"E42"),sQuery(id+"F6.wireOp",EDGE,"E47.0"),sQuery(id+"F6.wireOp",EDGE,"E48")])]}),"instanceName":"7"}),makeQuery(id+"F8.opPattern","SPLIT",FACE,{"disambiguationData":[OD(7.0)],"derivedFrom":makeQuery(id+"F1.opRevolve","SWEPT_FACE",FACE,{"disambiguationData":[OSD([sQuery(id+"F0.wireOp",EDGE,"E21")])]})})],"blendedInto":[makeQuery(id+"F8.opPattern","SPLIT",FACE,{"disambiguationData":[OD(7.0)],"derivedFrom":makeQuery(id+"F1.opRevolve","SWEPT_FACE",FACE,{"disambiguationData":[OSD([sQuery(id+"F0.wireOp",EDGE,"E21")])]})})]});
            var Q25;
            Q25=makeQuery(id+"F8.opPattern","COPY",EDGE,{"derivedFrom":makeQuery(id+"F7.boolean.opBoolean","INTERSECT",EDGE,{"derivedFrom":[makeQuery(id+"F1.opRevolve","SWEPT_FACE",FACE,{"disambiguationData":[OSD([sQuery(id+"F0.wireOp",EDGE,"E21")])]}),makeQuery(id+"F7.opLoft","SWEPT_FACE",FACE,{"disambiguationData":[OSD([sQuery(id+"F4.wireOp",EDGE,"E40.0"),sQuery(id+"F4.wireOp",EDGE,"E40.1"),sQuery(id+"F4.wireOp",EDGE,"E40.2"),sQuery(id+"F6.wireOp",EDGE,"E47.0"),sQuery(id+"F6.wireOp",EDGE,"E47.1"),sQuery(id+"F6.wireOp",EDGE,"E47.2")])]})]}),"instanceName":"7"});
            var Q26;
            Q26=makeQuery(id+"F8.opPattern","COPY",EDGE,{"derivedFrom":makeQuery(id+"F7.boolean.opBoolean","INTERSECT",EDGE,{"derivedFrom":[makeQuery(id+"F1.opRevolve","SWEPT_FACE",FACE,{"disambiguationData":[OSD([sQuery(id+"F0.wireOp",EDGE,"E21")])]}),makeQuery(id+"F7.opLoft","SWEPT_FACE",FACE,{"disambiguationData":[OSD([sQuery(id+"F4.wireOp",EDGE,"E40.1"),sQuery(id+"F4.wireOp",EDGE,"E40.2"),sQuery(id+"F4.wireOp",EDGE,"E41"),sQuery(id+"F6.wireOp",EDGE,"E47.1"),sQuery(id+"F6.wireOp",EDGE,"E47.2"),sQuery(id+"F6.wireOp",EDGE,"E51")])]})]}),"instanceName":"7"});
            var Q27;
            Q27=makeQuery(id+"F8.opPattern","COPY",EDGE,{"derivedFrom":makeQuery(id+"F7.boolean.opBoolean","INTERSECT",EDGE,{"derivedFrom":[makeQuery(id+"F1.opRevolve","SWEPT_FACE",FACE,{"disambiguationData":[OSD([sQuery(id+"F0.wireOp",EDGE,"E20")])]}),makeQuery(id+"F7.opLoft","SWEPT_FACE",FACE,{"disambiguationData":[OSD([sQuery(id+"F4.wireOp",EDGE,"E40.1"),sQuery(id+"F4.wireOp",EDGE,"E40.2"),sQuery(id+"F4.wireOp",EDGE,"E41"),sQuery(id+"F6.wireOp",EDGE,"E47.1"),sQuery(id+"F6.wireOp",EDGE,"E47.2"),sQuery(id+"F6.wireOp",EDGE,"E51")])]})]}),"instanceName":"7"});
            var Q28;
            Q28=makeQuery(id+"F8.opPattern","COPY",EDGE,{"derivedFrom":makeQuery(id+"F7.boolean.opBoolean","INTERSECT",EDGE,{"derivedFrom":[makeQuery(id+"F1.opRevolve","SWEPT_FACE",FACE,{"disambiguationData":[OSD([sQuery(id+"F0.wireOp",EDGE,"E20")])]}),makeQuery(id+"F7.opLoft","SWEPT_FACE",FACE,{"disambiguationData":[OSD([sQuery(id+"F4.wireOp",EDGE,"E36"),sQuery(id+"F4.wireOp",EDGE,"E40.2"),sQuery(id+"F4.wireOp",EDGE,"E41"),sQuery(id+"F6.wireOp",EDGE,"E44"),sQuery(id+"F6.wireOp",EDGE,"E47.2"),sQuery(id+"F6.wireOp",EDGE,"E51")])]})]}),"instanceName":"7"});
            var Q29;
            Q29=makeQuery(id+"F8.opPattern","COPY",EDGE,{"derivedFrom":makeQuery(id+"F7.boolean.opBoolean","INTERSECT",EDGE,{"derivedFrom":[makeQuery(id+"F1.opRevolve","SWEPT_FACE",FACE,{"disambiguationData":[OSD([sQuery(id+"F0.wireOp",EDGE,"E20")])]}),makeQuery(id+"F7.opLoft","SWEPT_FACE",FACE,{"disambiguationData":[OSD([sQuery(id+"F4.wireOp",EDGE,"E36"),sQuery(id+"F4.wireOp",EDGE,"E39.filletArc"),sQuery(id+"F4.wireOp",EDGE,"E41"),sQuery(id+"F6.wireOp",EDGE,"E44"),sQuery(id+"F6.wireOp",EDGE,"E46"),sQuery(id+"F6.wireOp",EDGE,"E51")])]})]}),"instanceName":"7"});
            fillet(context, id + "F15", {"entities" : qUnion([Q0, Q1, Q2, Q3, Q4, Q5, Q6, Q7, Q8, Q9, Q10, Q11, Q12, Q13, Q14, Q15, Q16, Q17, Q18, Q19, Q20, Q21, Q22, Q23, Q24, Q25, Q26, Q27, Q28, Q29]), "radius" : 1 * mm, "tangentPropagation" : true, "allowEdgeOverflow" : false});
        }
        {
            var Q0;
            Q0=makeQuery(id+"F8.opPattern","COPY",EDGE,{"derivedFrom":makeQuery(id+"F7.boolean.opBoolean","INTERSECT",EDGE,{"derivedFrom":[makeQuery(id+"F1.opRevolve","SWEPT_FACE",FACE,{"disambiguationData":[OSD([sQuery(id+"F0.wireOp",EDGE,"E21")])]}),makeQuery(id+"F7.opLoft","SWEPT_FACE",FACE,{"disambiguationData":[OSD([sQuery(id+"F4.wireOp",EDGE,"E36"),sQuery(id+"F4.wireOp",EDGE,"E39.filletArc"),sQuery(id+"F4.wireOp",EDGE,"E41"),sQuery(id+"F6.wireOp",EDGE,"E44"),sQuery(id+"F6.wireOp",EDGE,"E46"),sQuery(id+"F6.wireOp",EDGE,"E51")])]})]}),"instanceName":"8"});
            var Q1;
            Q1=makeQuery(id+"F8.opPattern","COPY",EDGE,{"derivedFrom":makeQuery(id+"F7.boolean.opBoolean","INTERSECT",EDGE,{"derivedFrom":[makeQuery(id+"F1.opRevolve","SWEPT_FACE",FACE,{"disambiguationData":[OSD([sQuery(id+"F0.wireOp",EDGE,"E21")])]}),makeQuery(id+"F7.opLoft","SWEPT_FACE",FACE,{"disambiguationData":[OSD([sQuery(id+"F4.wireOp",EDGE,"E38"),sQuery(id+"F4.wireOp",EDGE,"E39.filletArc"),sQuery(id+"F4.wireOp",EDGE,"E42"),sQuery(id+"F6.wireOp",EDGE,"E45"),sQuery(id+"F6.wireOp",EDGE,"E46"),sQuery(id+"F6.wireOp",EDGE,"E48")])]})]}),"instanceName":"8"});
            var Q2;
            Q2=makeQuery(id+"F13.opFillet","BLEND_EDGE",EDGE,{"blendedFrom":[makeQuery(id+"F8.opPattern","COPY",EDGE,{"derivedFrom":makeQuery(id+"F7.opLoft","SWEPT_EDGE",EDGE,{"disambiguationData":[OSD([sQuery(id+"F4.wireOp",EDGE,"E38"),sQuery(id+"F4.wireOp",EDGE,"E42"),sQuery(id+"F6.wireOp",EDGE,"E45"),sQuery(id+"F6.wireOp",EDGE,"E48")])]}),"instanceName":"8"}),makeQuery(id+"F8.opPattern","SPLIT",FACE,{"disambiguationData":[OD(9.0)],"derivedFrom":makeQuery(id+"F1.opRevolve","SWEPT_FACE",FACE,{"disambiguationData":[OSD([sQuery(id+"F0.wireOp",EDGE,"E21")])]})})],"blendedInto":[makeQuery(id+"F8.opPattern","SPLIT",FACE,{"disambiguationData":[OD(9.0)],"derivedFrom":makeQuery(id+"F1.opRevolve","SWEPT_FACE",FACE,{"disambiguationData":[OSD([sQuery(id+"F0.wireOp",EDGE,"E21")])]})})]});
            var Q3;
            Q3=makeQuery(id+"F8.opPattern","COPY",EDGE,{"derivedFrom":makeQuery(id+"F7.boolean.opBoolean","SPLIT",EDGE,{"disambiguationData":[OD(1.0)],"derivedFrom":makeQuery(id+"F1.opRevolve","SWEPT_EDGE",EDGE,{"disambiguationData":[OSD([sQuery(id+"F0.wireOp",EDGE,"E16"),sQuery(id+"F0.wireOp",EDGE,"E21")])]})}),"instanceName":"8"});
            var Q4;
            Q4=makeQuery(id+"F14.opFillet","BLEND_EDGE",EDGE,{"blendedFrom":[makeQuery(id+"F8.opPattern","COPY",EDGE,{"derivedFrom":makeQuery(id+"F7.opLoft","SWEPT_EDGE",EDGE,{"disambiguationData":[OSD([sQuery(id+"F4.wireOp",EDGE,"E40.0"),sQuery(id+"F4.wireOp",EDGE,"E42"),sQuery(id+"F6.wireOp",EDGE,"E47.0"),sQuery(id+"F6.wireOp",EDGE,"E48")])]}),"instanceName":"8"}),makeQuery(id+"F8.opPattern","SPLIT",FACE,{"disambiguationData":[OD(8.0)],"derivedFrom":makeQuery(id+"F1.opRevolve","SWEPT_FACE",FACE,{"disambiguationData":[OSD([sQuery(id+"F0.wireOp",EDGE,"E21")])]})})],"blendedInto":[makeQuery(id+"F8.opPattern","SPLIT",FACE,{"disambiguationData":[OD(8.0)],"derivedFrom":makeQuery(id+"F1.opRevolve","SWEPT_FACE",FACE,{"disambiguationData":[OSD([sQuery(id+"F0.wireOp",EDGE,"E21")])]})})]});
            var Q5;
            Q5=makeQuery(id+"F8.opPattern","COPY",EDGE,{"derivedFrom":makeQuery(id+"F7.boolean.opBoolean","INTERSECT",EDGE,{"derivedFrom":[makeQuery(id+"F1.opRevolve","SWEPT_FACE",FACE,{"disambiguationData":[OSD([sQuery(id+"F0.wireOp",EDGE,"E21")])]}),makeQuery(id+"F7.opLoft","SWEPT_FACE",FACE,{"disambiguationData":[OSD([sQuery(id+"F4.wireOp",EDGE,"E40.0"),sQuery(id+"F4.wireOp",EDGE,"E40.1"),sQuery(id+"F4.wireOp",EDGE,"E40.2"),sQuery(id+"F6.wireOp",EDGE,"E47.0"),sQuery(id+"F6.wireOp",EDGE,"E47.1"),sQuery(id+"F6.wireOp",EDGE,"E47.2")])]})]}),"instanceName":"8"});
            var Q6;
            Q6=makeQuery(id+"F8.opPattern","COPY",EDGE,{"derivedFrom":makeQuery(id+"F7.boolean.opBoolean","INTERSECT",EDGE,{"derivedFrom":[makeQuery(id+"F1.opRevolve","SWEPT_FACE",FACE,{"disambiguationData":[OSD([sQuery(id+"F0.wireOp",EDGE,"E21")])]}),makeQuery(id+"F7.opLoft","SWEPT_FACE",FACE,{"disambiguationData":[OSD([sQuery(id+"F4.wireOp",EDGE,"E40.1"),sQuery(id+"F4.wireOp",EDGE,"E40.2"),sQuery(id+"F4.wireOp",EDGE,"E41"),sQuery(id+"F6.wireOp",EDGE,"E47.1"),sQuery(id+"F6.wireOp",EDGE,"E47.2"),sQuery(id+"F6.wireOp",EDGE,"E51")])]})]}),"instanceName":"8"});
            var Q7;
            Q7=makeQuery(id+"F8.opPattern","COPY",EDGE,{"derivedFrom":makeQuery(id+"F7.boolean.opBoolean","INTERSECT",EDGE,{"derivedFrom":[makeQuery(id+"F1.opRevolve","SWEPT_FACE",FACE,{"disambiguationData":[OSD([sQuery(id+"F0.wireOp",EDGE,"E20")])]}),makeQuery(id+"F7.opLoft","SWEPT_FACE",FACE,{"disambiguationData":[OSD([sQuery(id+"F4.wireOp",EDGE,"E40.1"),sQuery(id+"F4.wireOp",EDGE,"E40.2"),sQuery(id+"F4.wireOp",EDGE,"E41"),sQuery(id+"F6.wireOp",EDGE,"E47.1"),sQuery(id+"F6.wireOp",EDGE,"E47.2"),sQuery(id+"F6.wireOp",EDGE,"E51")])]})]}),"instanceName":"8"});
            var Q8;
            Q8=makeQuery(id+"F8.opPattern","COPY",EDGE,{"derivedFrom":makeQuery(id+"F7.boolean.opBoolean","INTERSECT",EDGE,{"derivedFrom":[makeQuery(id+"F1.opRevolve","SWEPT_FACE",FACE,{"disambiguationData":[OSD([sQuery(id+"F0.wireOp",EDGE,"E20")])]}),makeQuery(id+"F7.opLoft","SWEPT_FACE",FACE,{"disambiguationData":[OSD([sQuery(id+"F4.wireOp",EDGE,"E36"),sQuery(id+"F4.wireOp",EDGE,"E40.2"),sQuery(id+"F4.wireOp",EDGE,"E41"),sQuery(id+"F6.wireOp",EDGE,"E44"),sQuery(id+"F6.wireOp",EDGE,"E47.2"),sQuery(id+"F6.wireOp",EDGE,"E51")])]})]}),"instanceName":"8"});
            var Q9;
            Q9=makeQuery(id+"F8.opPattern","COPY",EDGE,{"derivedFrom":makeQuery(id+"F7.boolean.opBoolean","INTERSECT",EDGE,{"derivedFrom":[makeQuery(id+"F1.opRevolve","SWEPT_FACE",FACE,{"disambiguationData":[OSD([sQuery(id+"F0.wireOp",EDGE,"E20")])]}),makeQuery(id+"F7.opLoft","SWEPT_FACE",FACE,{"disambiguationData":[OSD([sQuery(id+"F4.wireOp",EDGE,"E36"),sQuery(id+"F4.wireOp",EDGE,"E39.filletArc"),sQuery(id+"F4.wireOp",EDGE,"E41"),sQuery(id+"F6.wireOp",EDGE,"E44"),sQuery(id+"F6.wireOp",EDGE,"E46"),sQuery(id+"F6.wireOp",EDGE,"E51")])]})]}),"instanceName":"8"});
            var Q10;
            Q10=makeQuery(id+"F8.opPattern","COPY",EDGE,{"derivedFrom":makeQuery(id+"F7.boolean.opBoolean","INTERSECT",EDGE,{"derivedFrom":[makeQuery(id+"F1.opRevolve","SWEPT_FACE",FACE,{"disambiguationData":[OSD([sQuery(id+"F0.wireOp",EDGE,"E20")])]}),makeQuery(id+"F7.opLoft","SWEPT_FACE",FACE,{"disambiguationData":[OSD([sQuery(id+"F4.wireOp",EDGE,"E36"),sQuery(id+"F4.wireOp",EDGE,"E39.filletArc"),sQuery(id+"F4.wireOp",EDGE,"E41"),sQuery(id+"F6.wireOp",EDGE,"E44"),sQuery(id+"F6.wireOp",EDGE,"E46"),sQuery(id+"F6.wireOp",EDGE,"E51")])]})]}),"instanceName":"9"});
            var Q11;
            Q11=makeQuery(id+"F8.opPattern","COPY",EDGE,{"derivedFrom":makeQuery(id+"F7.boolean.opBoolean","INTERSECT",EDGE,{"derivedFrom":[makeQuery(id+"F1.opRevolve","SWEPT_FACE",FACE,{"disambiguationData":[OSD([sQuery(id+"F0.wireOp",EDGE,"E21")])]}),makeQuery(id+"F7.opLoft","SWEPT_FACE",FACE,{"disambiguationData":[OSD([sQuery(id+"F4.wireOp",EDGE,"E36"),sQuery(id+"F4.wireOp",EDGE,"E39.filletArc"),sQuery(id+"F4.wireOp",EDGE,"E41"),sQuery(id+"F6.wireOp",EDGE,"E44"),sQuery(id+"F6.wireOp",EDGE,"E46"),sQuery(id+"F6.wireOp",EDGE,"E51")])]})]}),"instanceName":"9"});
            var Q12;
            Q12=makeQuery(id+"F8.opPattern","COPY",EDGE,{"derivedFrom":makeQuery(id+"F7.boolean.opBoolean","INTERSECT",EDGE,{"derivedFrom":[makeQuery(id+"F1.opRevolve","SWEPT_FACE",FACE,{"disambiguationData":[OSD([sQuery(id+"F0.wireOp",EDGE,"E21")])]}),makeQuery(id+"F7.opLoft","SWEPT_FACE",FACE,{"disambiguationData":[OSD([sQuery(id+"F4.wireOp",EDGE,"E38"),sQuery(id+"F4.wireOp",EDGE,"E39.filletArc"),sQuery(id+"F4.wireOp",EDGE,"E42"),sQuery(id+"F6.wireOp",EDGE,"E45"),sQuery(id+"F6.wireOp",EDGE,"E46"),sQuery(id+"F6.wireOp",EDGE,"E48")])]})]}),"instanceName":"9"});
            var Q13;
            Q13=makeQuery(id+"F13.opFillet","BLEND_EDGE",EDGE,{"blendedFrom":[makeQuery(id+"F8.opPattern","COPY",EDGE,{"derivedFrom":makeQuery(id+"F7.opLoft","SWEPT_EDGE",EDGE,{"disambiguationData":[OSD([sQuery(id+"F4.wireOp",EDGE,"E38"),sQuery(id+"F4.wireOp",EDGE,"E42"),sQuery(id+"F6.wireOp",EDGE,"E45"),sQuery(id+"F6.wireOp",EDGE,"E48")])]}),"instanceName":"9"}),makeQuery(id+"F8.opPattern","SPLIT",FACE,{"disambiguationData":[OD(10.0)],"derivedFrom":makeQuery(id+"F1.opRevolve","SWEPT_FACE",FACE,{"disambiguationData":[OSD([sQuery(id+"F0.wireOp",EDGE,"E21")])]})})],"blendedInto":[makeQuery(id+"F8.opPattern","SPLIT",FACE,{"disambiguationData":[OD(10.0)],"derivedFrom":makeQuery(id+"F1.opRevolve","SWEPT_FACE",FACE,{"disambiguationData":[OSD([sQuery(id+"F0.wireOp",EDGE,"E21")])]})})]});
            var Q14;
            Q14=makeQuery(id+"F8.opPattern","COPY",EDGE,{"derivedFrom":makeQuery(id+"F7.boolean.opBoolean","SPLIT",EDGE,{"disambiguationData":[OD(1.0)],"derivedFrom":makeQuery(id+"F1.opRevolve","SWEPT_EDGE",EDGE,{"disambiguationData":[OSD([sQuery(id+"F0.wireOp",EDGE,"E16"),sQuery(id+"F0.wireOp",EDGE,"E21")])]})}),"instanceName":"9"});
            var Q15;
            Q15=makeQuery(id+"F14.opFillet","BLEND_EDGE",EDGE,{"blendedFrom":[makeQuery(id+"F8.opPattern","COPY",EDGE,{"derivedFrom":makeQuery(id+"F7.opLoft","SWEPT_EDGE",EDGE,{"disambiguationData":[OSD([sQuery(id+"F4.wireOp",EDGE,"E40.0"),sQuery(id+"F4.wireOp",EDGE,"E42"),sQuery(id+"F6.wireOp",EDGE,"E47.0"),sQuery(id+"F6.wireOp",EDGE,"E48")])]}),"instanceName":"9"}),makeQuery(id+"F8.opPattern","SPLIT",FACE,{"disambiguationData":[OD(9.0)],"derivedFrom":makeQuery(id+"F1.opRevolve","SWEPT_FACE",FACE,{"disambiguationData":[OSD([sQuery(id+"F0.wireOp",EDGE,"E21")])]})})],"blendedInto":[makeQuery(id+"F8.opPattern","SPLIT",FACE,{"disambiguationData":[OD(9.0)],"derivedFrom":makeQuery(id+"F1.opRevolve","SWEPT_FACE",FACE,{"disambiguationData":[OSD([sQuery(id+"F0.wireOp",EDGE,"E21")])]})})]});
            var Q16;
            Q16=makeQuery(id+"F8.opPattern","COPY",EDGE,{"derivedFrom":makeQuery(id+"F7.boolean.opBoolean","INTERSECT",EDGE,{"derivedFrom":[makeQuery(id+"F1.opRevolve","SWEPT_FACE",FACE,{"disambiguationData":[OSD([sQuery(id+"F0.wireOp",EDGE,"E21")])]}),makeQuery(id+"F7.opLoft","SWEPT_FACE",FACE,{"disambiguationData":[OSD([sQuery(id+"F4.wireOp",EDGE,"E40.0"),sQuery(id+"F4.wireOp",EDGE,"E40.1"),sQuery(id+"F4.wireOp",EDGE,"E40.2"),sQuery(id+"F6.wireOp",EDGE,"E47.0"),sQuery(id+"F6.wireOp",EDGE,"E47.1"),sQuery(id+"F6.wireOp",EDGE,"E47.2")])]})]}),"instanceName":"9"});
            var Q17;
            Q17=makeQuery(id+"F8.opPattern","COPY",EDGE,{"derivedFrom":makeQuery(id+"F7.boolean.opBoolean","INTERSECT",EDGE,{"derivedFrom":[makeQuery(id+"F1.opRevolve","SWEPT_FACE",FACE,{"disambiguationData":[OSD([sQuery(id+"F0.wireOp",EDGE,"E21")])]}),makeQuery(id+"F7.opLoft","SWEPT_FACE",FACE,{"disambiguationData":[OSD([sQuery(id+"F4.wireOp",EDGE,"E40.1"),sQuery(id+"F4.wireOp",EDGE,"E40.2"),sQuery(id+"F4.wireOp",EDGE,"E41"),sQuery(id+"F6.wireOp",EDGE,"E47.1"),sQuery(id+"F6.wireOp",EDGE,"E47.2"),sQuery(id+"F6.wireOp",EDGE,"E51")])]})]}),"instanceName":"9"});
            var Q18;
            Q18=makeQuery(id+"F8.opPattern","COPY",EDGE,{"derivedFrom":makeQuery(id+"F7.boolean.opBoolean","INTERSECT",EDGE,{"derivedFrom":[makeQuery(id+"F1.opRevolve","SWEPT_FACE",FACE,{"disambiguationData":[OSD([sQuery(id+"F0.wireOp",EDGE,"E20")])]}),makeQuery(id+"F7.opLoft","SWEPT_FACE",FACE,{"disambiguationData":[OSD([sQuery(id+"F4.wireOp",EDGE,"E40.1"),sQuery(id+"F4.wireOp",EDGE,"E40.2"),sQuery(id+"F4.wireOp",EDGE,"E41"),sQuery(id+"F6.wireOp",EDGE,"E47.1"),sQuery(id+"F6.wireOp",EDGE,"E47.2"),sQuery(id+"F6.wireOp",EDGE,"E51")])]})]}),"instanceName":"9"});
            var Q19;
            Q19=makeQuery(id+"F8.opPattern","COPY",EDGE,{"derivedFrom":makeQuery(id+"F7.boolean.opBoolean","INTERSECT",EDGE,{"derivedFrom":[makeQuery(id+"F1.opRevolve","SWEPT_FACE",FACE,{"disambiguationData":[OSD([sQuery(id+"F0.wireOp",EDGE,"E20")])]}),makeQuery(id+"F7.opLoft","SWEPT_FACE",FACE,{"disambiguationData":[OSD([sQuery(id+"F4.wireOp",EDGE,"E36"),sQuery(id+"F4.wireOp",EDGE,"E40.2"),sQuery(id+"F4.wireOp",EDGE,"E41"),sQuery(id+"F6.wireOp",EDGE,"E44"),sQuery(id+"F6.wireOp",EDGE,"E47.2"),sQuery(id+"F6.wireOp",EDGE,"E51")])]})]}),"instanceName":"9"});
            var Q20;
            Q20=makeQuery(id+"F8.opPattern","COPY",EDGE,{"derivedFrom":makeQuery(id+"F7.boolean.opBoolean","INTERSECT",EDGE,{"derivedFrom":[makeQuery(id+"F1.opRevolve","SWEPT_FACE",FACE,{"disambiguationData":[OSD([sQuery(id+"F0.wireOp",EDGE,"E21")])]}),makeQuery(id+"F7.opLoft","SWEPT_FACE",FACE,{"disambiguationData":[OSD([sQuery(id+"F4.wireOp",EDGE,"E40.1"),sQuery(id+"F4.wireOp",EDGE,"E40.2"),sQuery(id+"F4.wireOp",EDGE,"E41"),sQuery(id+"F6.wireOp",EDGE,"E47.1"),sQuery(id+"F6.wireOp",EDGE,"E47.2"),sQuery(id+"F6.wireOp",EDGE,"E51")])]})]}),"instanceName":"10"});
            var Q21;
            Q21=makeQuery(id+"F8.opPattern","COPY",EDGE,{"derivedFrom":makeQuery(id+"F7.boolean.opBoolean","INTERSECT",EDGE,{"derivedFrom":[makeQuery(id+"F1.opRevolve","SWEPT_FACE",FACE,{"disambiguationData":[OSD([sQuery(id+"F0.wireOp",EDGE,"E21")])]}),makeQuery(id+"F7.opLoft","SWEPT_FACE",FACE,{"disambiguationData":[OSD([sQuery(id+"F4.wireOp",EDGE,"E40.0"),sQuery(id+"F4.wireOp",EDGE,"E40.1"),sQuery(id+"F4.wireOp",EDGE,"E40.2"),sQuery(id+"F6.wireOp",EDGE,"E47.0"),sQuery(id+"F6.wireOp",EDGE,"E47.1"),sQuery(id+"F6.wireOp",EDGE,"E47.2")])]})]}),"instanceName":"10"});
            var Q22;
            Q22=makeQuery(id+"F14.opFillet","BLEND_EDGE",EDGE,{"blendedFrom":[makeQuery(id+"F8.opPattern","COPY",EDGE,{"derivedFrom":makeQuery(id+"F7.opLoft","SWEPT_EDGE",EDGE,{"disambiguationData":[OSD([sQuery(id+"F4.wireOp",EDGE,"E40.0"),sQuery(id+"F4.wireOp",EDGE,"E42"),sQuery(id+"F6.wireOp",EDGE,"E47.0"),sQuery(id+"F6.wireOp",EDGE,"E48")])]}),"instanceName":"10"}),makeQuery(id+"F8.opPattern","SPLIT",FACE,{"disambiguationData":[OD(10.0)],"derivedFrom":makeQuery(id+"F1.opRevolve","SWEPT_FACE",FACE,{"disambiguationData":[OSD([sQuery(id+"F0.wireOp",EDGE,"E21")])]})})],"blendedInto":[makeQuery(id+"F8.opPattern","SPLIT",FACE,{"disambiguationData":[OD(10.0)],"derivedFrom":makeQuery(id+"F1.opRevolve","SWEPT_FACE",FACE,{"disambiguationData":[OSD([sQuery(id+"F0.wireOp",EDGE,"E21")])]})})]});
            var Q23;
            Q23=makeQuery(id+"F8.opPattern","COPY",EDGE,{"derivedFrom":makeQuery(id+"F7.boolean.opBoolean","SPLIT",EDGE,{"disambiguationData":[OD(1.0)],"derivedFrom":makeQuery(id+"F1.opRevolve","SWEPT_EDGE",EDGE,{"disambiguationData":[OSD([sQuery(id+"F0.wireOp",EDGE,"E16"),sQuery(id+"F0.wireOp",EDGE,"E21")])]})}),"instanceName":"10"});
            var Q24;
            Q24=makeQuery(id+"F13.opFillet","BLEND_EDGE",EDGE,{"blendedFrom":[makeQuery(id+"F8.opPattern","COPY",EDGE,{"derivedFrom":makeQuery(id+"F7.opLoft","SWEPT_EDGE",EDGE,{"disambiguationData":[OSD([sQuery(id+"F4.wireOp",EDGE,"E38"),sQuery(id+"F4.wireOp",EDGE,"E42"),sQuery(id+"F6.wireOp",EDGE,"E45"),sQuery(id+"F6.wireOp",EDGE,"E48")])]}),"instanceName":"10"}),makeQuery(id+"F8.opPattern","SPLIT",FACE,{"disambiguationData":[OD(11.0)],"derivedFrom":makeQuery(id+"F1.opRevolve","SWEPT_FACE",FACE,{"disambiguationData":[OSD([sQuery(id+"F0.wireOp",EDGE,"E21")])]})})],"blendedInto":[makeQuery(id+"F8.opPattern","SPLIT",FACE,{"disambiguationData":[OD(11.0)],"derivedFrom":makeQuery(id+"F1.opRevolve","SWEPT_FACE",FACE,{"disambiguationData":[OSD([sQuery(id+"F0.wireOp",EDGE,"E21")])]})})]});
            var Q25;
            Q25=makeQuery(id+"F8.opPattern","COPY",EDGE,{"derivedFrom":makeQuery(id+"F7.boolean.opBoolean","INTERSECT",EDGE,{"derivedFrom":[makeQuery(id+"F1.opRevolve","SWEPT_FACE",FACE,{"disambiguationData":[OSD([sQuery(id+"F0.wireOp",EDGE,"E21")])]}),makeQuery(id+"F7.opLoft","SWEPT_FACE",FACE,{"disambiguationData":[OSD([sQuery(id+"F4.wireOp",EDGE,"E38"),sQuery(id+"F4.wireOp",EDGE,"E39.filletArc"),sQuery(id+"F4.wireOp",EDGE,"E42"),sQuery(id+"F6.wireOp",EDGE,"E45"),sQuery(id+"F6.wireOp",EDGE,"E46"),sQuery(id+"F6.wireOp",EDGE,"E48")])]})]}),"instanceName":"10"});
            var Q26;
            Q26=makeQuery(id+"F8.opPattern","COPY",EDGE,{"derivedFrom":makeQuery(id+"F7.boolean.opBoolean","INTERSECT",EDGE,{"derivedFrom":[makeQuery(id+"F1.opRevolve","SWEPT_FACE",FACE,{"disambiguationData":[OSD([sQuery(id+"F0.wireOp",EDGE,"E21")])]}),makeQuery(id+"F7.opLoft","SWEPT_FACE",FACE,{"disambiguationData":[OSD([sQuery(id+"F4.wireOp",EDGE,"E36"),sQuery(id+"F4.wireOp",EDGE,"E39.filletArc"),sQuery(id+"F4.wireOp",EDGE,"E41"),sQuery(id+"F6.wireOp",EDGE,"E44"),sQuery(id+"F6.wireOp",EDGE,"E46"),sQuery(id+"F6.wireOp",EDGE,"E51")])]})]}),"instanceName":"10"});
            var Q27;
            Q27=makeQuery(id+"F8.opPattern","COPY",EDGE,{"derivedFrom":makeQuery(id+"F7.boolean.opBoolean","INTERSECT",EDGE,{"derivedFrom":[makeQuery(id+"F1.opRevolve","SWEPT_FACE",FACE,{"disambiguationData":[OSD([sQuery(id+"F0.wireOp",EDGE,"E20")])]}),makeQuery(id+"F7.opLoft","SWEPT_FACE",FACE,{"disambiguationData":[OSD([sQuery(id+"F4.wireOp",EDGE,"E36"),sQuery(id+"F4.wireOp",EDGE,"E39.filletArc"),sQuery(id+"F4.wireOp",EDGE,"E41"),sQuery(id+"F6.wireOp",EDGE,"E44"),sQuery(id+"F6.wireOp",EDGE,"E46"),sQuery(id+"F6.wireOp",EDGE,"E51")])]})]}),"instanceName":"10"});
            var Q28;
            Q28=makeQuery(id+"F8.opPattern","COPY",EDGE,{"derivedFrom":makeQuery(id+"F7.boolean.opBoolean","INTERSECT",EDGE,{"derivedFrom":[makeQuery(id+"F1.opRevolve","SWEPT_FACE",FACE,{"disambiguationData":[OSD([sQuery(id+"F0.wireOp",EDGE,"E20")])]}),makeQuery(id+"F7.opLoft","SWEPT_FACE",FACE,{"disambiguationData":[OSD([sQuery(id+"F4.wireOp",EDGE,"E36"),sQuery(id+"F4.wireOp",EDGE,"E40.2"),sQuery(id+"F4.wireOp",EDGE,"E41"),sQuery(id+"F6.wireOp",EDGE,"E44"),sQuery(id+"F6.wireOp",EDGE,"E47.2"),sQuery(id+"F6.wireOp",EDGE,"E51")])]})]}),"instanceName":"10"});
            var Q29;
            Q29=makeQuery(id+"F8.opPattern","COPY",EDGE,{"derivedFrom":makeQuery(id+"F7.boolean.opBoolean","INTERSECT",EDGE,{"derivedFrom":[makeQuery(id+"F1.opRevolve","SWEPT_FACE",FACE,{"disambiguationData":[OSD([sQuery(id+"F0.wireOp",EDGE,"E20")])]}),makeQuery(id+"F7.opLoft","SWEPT_FACE",FACE,{"disambiguationData":[OSD([sQuery(id+"F4.wireOp",EDGE,"E40.1"),sQuery(id+"F4.wireOp",EDGE,"E40.2"),sQuery(id+"F4.wireOp",EDGE,"E41"),sQuery(id+"F6.wireOp",EDGE,"E47.1"),sQuery(id+"F6.wireOp",EDGE,"E47.2"),sQuery(id+"F6.wireOp",EDGE,"E51")])]})]}),"instanceName":"10"});
            fillet(context, id + "F16", {"entities" : qUnion([Q0, Q1, Q2, Q3, Q4, Q5, Q6, Q7, Q8, Q9, Q10, Q11, Q12, Q13, Q14, Q15, Q16, Q17, Q18, Q19, Q20, Q21, Q22, Q23, Q24, Q25, Q26, Q27, Q28, Q29]), "radius" : 1 * mm, "tangentPropagation" : true, "allowEdgeOverflow" : false});
        }
        {
            var Q0;
            Q0=makeQuery(id+"F8.opPattern","COPY",EDGE,{"derivedFrom":makeQuery(id+"F7.boolean.opBoolean","INTERSECT",EDGE,{"derivedFrom":[makeQuery(id+"F1.opRevolve","SWEPT_FACE",FACE,{"disambiguationData":[OSD([sQuery(id+"F0.wireOp",EDGE,"E20")])]}),makeQuery(id+"F7.opLoft","SWEPT_FACE",FACE,{"disambiguationData":[OSD([sQuery(id+"F4.wireOp",EDGE,"E36"),sQuery(id+"F4.wireOp",EDGE,"E39.filletArc"),sQuery(id+"F4.wireOp",EDGE,"E41"),sQuery(id+"F6.wireOp",EDGE,"E44"),sQuery(id+"F6.wireOp",EDGE,"E46"),sQuery(id+"F6.wireOp",EDGE,"E51")])]})]}),"instanceName":"11"});
            var Q1;
            Q1=makeQuery(id+"F8.opPattern","COPY",EDGE,{"derivedFrom":makeQuery(id+"F7.boolean.opBoolean","INTERSECT",EDGE,{"derivedFrom":[makeQuery(id+"F1.opRevolve","SWEPT_FACE",FACE,{"disambiguationData":[OSD([sQuery(id+"F0.wireOp",EDGE,"E21")])]}),makeQuery(id+"F7.opLoft","SWEPT_FACE",FACE,{"disambiguationData":[OSD([sQuery(id+"F4.wireOp",EDGE,"E36"),sQuery(id+"F4.wireOp",EDGE,"E39.filletArc"),sQuery(id+"F4.wireOp",EDGE,"E41"),sQuery(id+"F6.wireOp",EDGE,"E44"),sQuery(id+"F6.wireOp",EDGE,"E46"),sQuery(id+"F6.wireOp",EDGE,"E51")])]})]}),"instanceName":"11"});
            var Q2;
            Q2=makeQuery(id+"F8.opPattern","COPY",EDGE,{"derivedFrom":makeQuery(id+"F7.boolean.opBoolean","INTERSECT",EDGE,{"derivedFrom":[makeQuery(id+"F1.opRevolve","SWEPT_FACE",FACE,{"disambiguationData":[OSD([sQuery(id+"F0.wireOp",EDGE,"E21")])]}),makeQuery(id+"F7.opLoft","SWEPT_FACE",FACE,{"disambiguationData":[OSD([sQuery(id+"F4.wireOp",EDGE,"E38"),sQuery(id+"F4.wireOp",EDGE,"E39.filletArc"),sQuery(id+"F4.wireOp",EDGE,"E42"),sQuery(id+"F6.wireOp",EDGE,"E45"),sQuery(id+"F6.wireOp",EDGE,"E46"),sQuery(id+"F6.wireOp",EDGE,"E48")])]})]}),"instanceName":"11"});
            var Q3;
            Q3=makeQuery(id+"F13.opFillet","BLEND_EDGE",EDGE,{"blendedFrom":[makeQuery(id+"F8.opPattern","COPY",EDGE,{"derivedFrom":makeQuery(id+"F7.opLoft","SWEPT_EDGE",EDGE,{"disambiguationData":[OSD([sQuery(id+"F4.wireOp",EDGE,"E38"),sQuery(id+"F4.wireOp",EDGE,"E42"),sQuery(id+"F6.wireOp",EDGE,"E45"),sQuery(id+"F6.wireOp",EDGE,"E48")])]}),"instanceName":"11"}),makeQuery(id+"F8.opPattern","SPLIT",FACE,{"disambiguationData":[OD(1.0)],"derivedFrom":makeQuery(id+"F1.opRevolve","SWEPT_FACE",FACE,{"disambiguationData":[OSD([sQuery(id+"F0.wireOp",EDGE,"E21")])]})})],"blendedInto":[makeQuery(id+"F8.opPattern","SPLIT",FACE,{"disambiguationData":[OD(1.0)],"derivedFrom":makeQuery(id+"F1.opRevolve","SWEPT_FACE",FACE,{"disambiguationData":[OSD([sQuery(id+"F0.wireOp",EDGE,"E21")])]})})]});
            var Q4;
            Q4=makeQuery(id+"F8.opPattern","COPY",EDGE,{"derivedFrom":makeQuery(id+"F7.boolean.opBoolean","SPLIT",EDGE,{"disambiguationData":[OD(1.0)],"derivedFrom":makeQuery(id+"F1.opRevolve","SWEPT_EDGE",EDGE,{"disambiguationData":[OSD([sQuery(id+"F0.wireOp",EDGE,"E16"),sQuery(id+"F0.wireOp",EDGE,"E21")])]})}),"instanceName":"11"});
            var Q5;
            Q5=makeQuery(id+"F14.opFillet","BLEND_EDGE",EDGE,{"blendedFrom":[makeQuery(id+"F8.opPattern","COPY",EDGE,{"derivedFrom":makeQuery(id+"F7.opLoft","SWEPT_EDGE",EDGE,{"disambiguationData":[OSD([sQuery(id+"F4.wireOp",EDGE,"E40.0"),sQuery(id+"F4.wireOp",EDGE,"E42"),sQuery(id+"F6.wireOp",EDGE,"E47.0"),sQuery(id+"F6.wireOp",EDGE,"E48")])]}),"instanceName":"11"}),makeQuery(id+"F8.opPattern","SPLIT",FACE,{"disambiguationData":[OD(11.0)],"derivedFrom":makeQuery(id+"F1.opRevolve","SWEPT_FACE",FACE,{"disambiguationData":[OSD([sQuery(id+"F0.wireOp",EDGE,"E21")])]})})],"blendedInto":[makeQuery(id+"F8.opPattern","SPLIT",FACE,{"disambiguationData":[OD(11.0)],"derivedFrom":makeQuery(id+"F1.opRevolve","SWEPT_FACE",FACE,{"disambiguationData":[OSD([sQuery(id+"F0.wireOp",EDGE,"E21")])]})})]});
            var Q6;
            Q6=makeQuery(id+"F8.opPattern","COPY",EDGE,{"derivedFrom":makeQuery(id+"F7.boolean.opBoolean","INTERSECT",EDGE,{"derivedFrom":[makeQuery(id+"F1.opRevolve","SWEPT_FACE",FACE,{"disambiguationData":[OSD([sQuery(id+"F0.wireOp",EDGE,"E21")])]}),makeQuery(id+"F7.opLoft","SWEPT_FACE",FACE,{"disambiguationData":[OSD([sQuery(id+"F4.wireOp",EDGE,"E40.0"),sQuery(id+"F4.wireOp",EDGE,"E40.1"),sQuery(id+"F4.wireOp",EDGE,"E40.2"),sQuery(id+"F6.wireOp",EDGE,"E47.0"),sQuery(id+"F6.wireOp",EDGE,"E47.1"),sQuery(id+"F6.wireOp",EDGE,"E47.2")])]})]}),"instanceName":"11"});
            var Q7;
            Q7=makeQuery(id+"F8.opPattern","COPY",EDGE,{"derivedFrom":makeQuery(id+"F7.boolean.opBoolean","INTERSECT",EDGE,{"derivedFrom":[makeQuery(id+"F1.opRevolve","SWEPT_FACE",FACE,{"disambiguationData":[OSD([sQuery(id+"F0.wireOp",EDGE,"E21")])]}),makeQuery(id+"F7.opLoft","SWEPT_FACE",FACE,{"disambiguationData":[OSD([sQuery(id+"F4.wireOp",EDGE,"E40.1"),sQuery(id+"F4.wireOp",EDGE,"E40.2"),sQuery(id+"F4.wireOp",EDGE,"E41"),sQuery(id+"F6.wireOp",EDGE,"E47.1"),sQuery(id+"F6.wireOp",EDGE,"E47.2"),sQuery(id+"F6.wireOp",EDGE,"E51")])]})]}),"instanceName":"11"});
            var Q8;
            Q8=makeQuery(id+"F8.opPattern","COPY",EDGE,{"derivedFrom":makeQuery(id+"F7.boolean.opBoolean","INTERSECT",EDGE,{"derivedFrom":[makeQuery(id+"F1.opRevolve","SWEPT_FACE",FACE,{"disambiguationData":[OSD([sQuery(id+"F0.wireOp",EDGE,"E20")])]}),makeQuery(id+"F7.opLoft","SWEPT_FACE",FACE,{"disambiguationData":[OSD([sQuery(id+"F4.wireOp",EDGE,"E40.1"),sQuery(id+"F4.wireOp",EDGE,"E40.2"),sQuery(id+"F4.wireOp",EDGE,"E41"),sQuery(id+"F6.wireOp",EDGE,"E47.1"),sQuery(id+"F6.wireOp",EDGE,"E47.2"),sQuery(id+"F6.wireOp",EDGE,"E51")])]})]}),"instanceName":"11"});
            var Q9;
            Q9=makeQuery(id+"F8.opPattern","COPY",EDGE,{"derivedFrom":makeQuery(id+"F7.boolean.opBoolean","INTERSECT",EDGE,{"derivedFrom":[makeQuery(id+"F1.opRevolve","SWEPT_FACE",FACE,{"disambiguationData":[OSD([sQuery(id+"F0.wireOp",EDGE,"E20")])]}),makeQuery(id+"F7.opLoft","SWEPT_FACE",FACE,{"disambiguationData":[OSD([sQuery(id+"F4.wireOp",EDGE,"E36"),sQuery(id+"F4.wireOp",EDGE,"E40.2"),sQuery(id+"F4.wireOp",EDGE,"E41"),sQuery(id+"F6.wireOp",EDGE,"E44"),sQuery(id+"F6.wireOp",EDGE,"E47.2"),sQuery(id+"F6.wireOp",EDGE,"E51")])]})]}),"instanceName":"11"});
            var Q10;
            Q10=makeQuery(id+"F7.boolean.opBoolean","INTERSECT",EDGE,{"derivedFrom":[makeQuery(id+"F1.opRevolve","SWEPT_FACE",FACE,{"disambiguationData":[OSD([sQuery(id+"F0.wireOp",EDGE,"E20")])]}),makeQuery(id+"F7.opLoft","SWEPT_FACE",FACE,{"disambiguationData":[OSD([sQuery(id+"F4.wireOp",EDGE,"E36"),sQuery(id+"F4.wireOp",EDGE,"E39.filletArc"),sQuery(id+"F4.wireOp",EDGE,"E41"),sQuery(id+"F6.wireOp",EDGE,"E44"),sQuery(id+"F6.wireOp",EDGE,"E46"),sQuery(id+"F6.wireOp",EDGE,"E51")])]})]});
            var Q11;
            Q11=makeQuery(id+"F7.boolean.opBoolean","INTERSECT",EDGE,{"derivedFrom":[makeQuery(id+"F1.opRevolve","SWEPT_FACE",FACE,{"disambiguationData":[OSD([sQuery(id+"F0.wireOp",EDGE,"E21")])]}),makeQuery(id+"F7.opLoft","SWEPT_FACE",FACE,{"disambiguationData":[OSD([sQuery(id+"F4.wireOp",EDGE,"E36"),sQuery(id+"F4.wireOp",EDGE,"E39.filletArc"),sQuery(id+"F4.wireOp",EDGE,"E41"),sQuery(id+"F6.wireOp",EDGE,"E44"),sQuery(id+"F6.wireOp",EDGE,"E46"),sQuery(id+"F6.wireOp",EDGE,"E51")])]})]});
            var Q12;
            Q12=makeQuery(id+"F7.boolean.opBoolean","INTERSECT",EDGE,{"derivedFrom":[makeQuery(id+"F1.opRevolve","SWEPT_FACE",FACE,{"disambiguationData":[OSD([sQuery(id+"F0.wireOp",EDGE,"E21")])]}),makeQuery(id+"F7.opLoft","SWEPT_FACE",FACE,{"disambiguationData":[OSD([sQuery(id+"F4.wireOp",EDGE,"E38"),sQuery(id+"F4.wireOp",EDGE,"E39.filletArc"),sQuery(id+"F4.wireOp",EDGE,"E42"),sQuery(id+"F6.wireOp",EDGE,"E45"),sQuery(id+"F6.wireOp",EDGE,"E46"),sQuery(id+"F6.wireOp",EDGE,"E48")])]})]});
            var Q13;
            Q13=makeQuery(id+"F13.opFillet","BLEND_EDGE",EDGE,{"blendedFrom":[makeQuery(id+"F7.opLoft","SWEPT_EDGE",EDGE,{"disambiguationData":[OSD([sQuery(id+"F4.wireOp",EDGE,"E38"),sQuery(id+"F4.wireOp",EDGE,"E42"),sQuery(id+"F6.wireOp",EDGE,"E45"),sQuery(id+"F6.wireOp",EDGE,"E48")])]}),makeQuery(id+"F8.opPattern","SPLIT",FACE,{"disambiguationData":[OD(0.0)],"derivedFrom":makeQuery(id+"F1.opRevolve","SWEPT_FACE",FACE,{"disambiguationData":[OSD([sQuery(id+"F0.wireOp",EDGE,"E21")])]})})],"blendedInto":[makeQuery(id+"F8.opPattern","SPLIT",FACE,{"disambiguationData":[OD(0.0)],"derivedFrom":makeQuery(id+"F1.opRevolve","SWEPT_FACE",FACE,{"disambiguationData":[OSD([sQuery(id+"F0.wireOp",EDGE,"E21")])]})})]});
            var Q14;
            Q14=makeQuery(id+"F7.boolean.opBoolean","SPLIT",EDGE,{"disambiguationData":[OD(1.0)],"derivedFrom":makeQuery(id+"F1.opRevolve","SWEPT_EDGE",EDGE,{"disambiguationData":[OSD([sQuery(id+"F0.wireOp",EDGE,"E16"),sQuery(id+"F0.wireOp",EDGE,"E21")])]})});
            var Q15;
            Q15=makeQuery(id+"F14.opFillet","BLEND_EDGE",EDGE,{"blendedFrom":[makeQuery(id+"F7.opLoft","SWEPT_EDGE",EDGE,{"disambiguationData":[OSD([sQuery(id+"F4.wireOp",EDGE,"E40.0"),sQuery(id+"F4.wireOp",EDGE,"E42"),sQuery(id+"F6.wireOp",EDGE,"E47.0"),sQuery(id+"F6.wireOp",EDGE,"E48")])]}),makeQuery(id+"F8.opPattern","SPLIT",FACE,{"disambiguationData":[OD(1.0)],"derivedFrom":makeQuery(id+"F1.opRevolve","SWEPT_FACE",FACE,{"disambiguationData":[OSD([sQuery(id+"F0.wireOp",EDGE,"E21")])]})})],"blendedInto":[makeQuery(id+"F8.opPattern","SPLIT",FACE,{"disambiguationData":[OD(1.0)],"derivedFrom":makeQuery(id+"F1.opRevolve","SWEPT_FACE",FACE,{"disambiguationData":[OSD([sQuery(id+"F0.wireOp",EDGE,"E21")])]})})]});
            var Q16;
            Q16=makeQuery(id+"F7.boolean.opBoolean","INTERSECT",EDGE,{"derivedFrom":[makeQuery(id+"F1.opRevolve","SWEPT_FACE",FACE,{"disambiguationData":[OSD([sQuery(id+"F0.wireOp",EDGE,"E21")])]}),makeQuery(id+"F7.opLoft","SWEPT_FACE",FACE,{"disambiguationData":[OSD([sQuery(id+"F4.wireOp",EDGE,"E40.0"),sQuery(id+"F4.wireOp",EDGE,"E40.1"),sQuery(id+"F4.wireOp",EDGE,"E40.2"),sQuery(id+"F6.wireOp",EDGE,"E47.0"),sQuery(id+"F6.wireOp",EDGE,"E47.1"),sQuery(id+"F6.wireOp",EDGE,"E47.2")])]})]});
            var Q17;
            Q17=makeQuery(id+"F7.boolean.opBoolean","INTERSECT",EDGE,{"derivedFrom":[makeQuery(id+"F1.opRevolve","SWEPT_FACE",FACE,{"disambiguationData":[OSD([sQuery(id+"F0.wireOp",EDGE,"E21")])]}),makeQuery(id+"F7.opLoft","SWEPT_FACE",FACE,{"disambiguationData":[OSD([sQuery(id+"F4.wireOp",EDGE,"E40.1"),sQuery(id+"F4.wireOp",EDGE,"E40.2"),sQuery(id+"F4.wireOp",EDGE,"E41"),sQuery(id+"F6.wireOp",EDGE,"E47.1"),sQuery(id+"F6.wireOp",EDGE,"E47.2"),sQuery(id+"F6.wireOp",EDGE,"E51")])]})]});
            var Q18;
            Q18=makeQuery(id+"F7.boolean.opBoolean","INTERSECT",EDGE,{"derivedFrom":[makeQuery(id+"F1.opRevolve","SWEPT_FACE",FACE,{"disambiguationData":[OSD([sQuery(id+"F0.wireOp",EDGE,"E20")])]}),makeQuery(id+"F7.opLoft","SWEPT_FACE",FACE,{"disambiguationData":[OSD([sQuery(id+"F4.wireOp",EDGE,"E36"),sQuery(id+"F4.wireOp",EDGE,"E40.2"),sQuery(id+"F4.wireOp",EDGE,"E41"),sQuery(id+"F6.wireOp",EDGE,"E44"),sQuery(id+"F6.wireOp",EDGE,"E47.2"),sQuery(id+"F6.wireOp",EDGE,"E51")])]})]});
            var Q19;
            Q19=makeQuery(id+"F7.boolean.opBoolean","INTERSECT",EDGE,{"derivedFrom":[makeQuery(id+"F1.opRevolve","SWEPT_FACE",FACE,{"disambiguationData":[OSD([sQuery(id+"F0.wireOp",EDGE,"E20")])]}),makeQuery(id+"F7.opLoft","SWEPT_FACE",FACE,{"disambiguationData":[OSD([sQuery(id+"F4.wireOp",EDGE,"E40.1"),sQuery(id+"F4.wireOp",EDGE,"E40.2"),sQuery(id+"F4.wireOp",EDGE,"E41"),sQuery(id+"F6.wireOp",EDGE,"E47.1"),sQuery(id+"F6.wireOp",EDGE,"E47.2"),sQuery(id+"F6.wireOp",EDGE,"E51")])]})]});
            var Q20;
            Q20=makeQuery(id+"F8.opPattern","COPY",EDGE,{"derivedFrom":makeQuery(id+"F7.boolean.opBoolean","INTERSECT",EDGE,{"derivedFrom":[makeQuery(id+"F1.opRevolve","SWEPT_FACE",FACE,{"disambiguationData":[OSD([sQuery(id+"F0.wireOp",EDGE,"E20")])]}),makeQuery(id+"F7.opLoft","SWEPT_FACE",FACE,{"disambiguationData":[OSD([sQuery(id+"F4.wireOp",EDGE,"E36"),sQuery(id+"F4.wireOp",EDGE,"E39.filletArc"),sQuery(id+"F4.wireOp",EDGE,"E41"),sQuery(id+"F6.wireOp",EDGE,"E44"),sQuery(id+"F6.wireOp",EDGE,"E46"),sQuery(id+"F6.wireOp",EDGE,"E51")])]})]}),"instanceName":"1"});
            var Q21;
            Q21=makeQuery(id+"F8.opPattern","COPY",EDGE,{"derivedFrom":makeQuery(id+"F7.boolean.opBoolean","INTERSECT",EDGE,{"derivedFrom":[makeQuery(id+"F1.opRevolve","SWEPT_FACE",FACE,{"disambiguationData":[OSD([sQuery(id+"F0.wireOp",EDGE,"E21")])]}),makeQuery(id+"F7.opLoft","SWEPT_FACE",FACE,{"disambiguationData":[OSD([sQuery(id+"F4.wireOp",EDGE,"E36"),sQuery(id+"F4.wireOp",EDGE,"E39.filletArc"),sQuery(id+"F4.wireOp",EDGE,"E41"),sQuery(id+"F6.wireOp",EDGE,"E44"),sQuery(id+"F6.wireOp",EDGE,"E46"),sQuery(id+"F6.wireOp",EDGE,"E51")])]})]}),"instanceName":"1"});
            var Q22;
            Q22=makeQuery(id+"F8.opPattern","COPY",EDGE,{"derivedFrom":makeQuery(id+"F7.boolean.opBoolean","INTERSECT",EDGE,{"derivedFrom":[makeQuery(id+"F1.opRevolve","SWEPT_FACE",FACE,{"disambiguationData":[OSD([sQuery(id+"F0.wireOp",EDGE,"E21")])]}),makeQuery(id+"F7.opLoft","SWEPT_FACE",FACE,{"disambiguationData":[OSD([sQuery(id+"F4.wireOp",EDGE,"E38"),sQuery(id+"F4.wireOp",EDGE,"E39.filletArc"),sQuery(id+"F4.wireOp",EDGE,"E42"),sQuery(id+"F6.wireOp",EDGE,"E45"),sQuery(id+"F6.wireOp",EDGE,"E46"),sQuery(id+"F6.wireOp",EDGE,"E48")])]})]}),"instanceName":"1"});
            var Q23;
            Q23=makeQuery(id+"F13.opFillet","BLEND_EDGE",EDGE,{"blendedFrom":[makeQuery(id+"F8.opPattern","COPY",EDGE,{"derivedFrom":makeQuery(id+"F7.opLoft","SWEPT_EDGE",EDGE,{"disambiguationData":[OSD([sQuery(id+"F4.wireOp",EDGE,"E38"),sQuery(id+"F4.wireOp",EDGE,"E42"),sQuery(id+"F6.wireOp",EDGE,"E45"),sQuery(id+"F6.wireOp",EDGE,"E48")])]}),"instanceName":"1"}),makeQuery(id+"F8.opPattern","SPLIT",FACE,{"disambiguationData":[OD(2.0)],"derivedFrom":makeQuery(id+"F1.opRevolve","SWEPT_FACE",FACE,{"disambiguationData":[OSD([sQuery(id+"F0.wireOp",EDGE,"E21")])]})})],"blendedInto":[makeQuery(id+"F8.opPattern","SPLIT",FACE,{"disambiguationData":[OD(2.0)],"derivedFrom":makeQuery(id+"F1.opRevolve","SWEPT_FACE",FACE,{"disambiguationData":[OSD([sQuery(id+"F0.wireOp",EDGE,"E21")])]})})]});
            var Q24;
            Q24=makeQuery(id+"F8.opPattern","COPY",EDGE,{"derivedFrom":makeQuery(id+"F7.boolean.opBoolean","SPLIT",EDGE,{"disambiguationData":[OD(1.0)],"derivedFrom":makeQuery(id+"F1.opRevolve","SWEPT_EDGE",EDGE,{"disambiguationData":[OSD([sQuery(id+"F0.wireOp",EDGE,"E16"),sQuery(id+"F0.wireOp",EDGE,"E21")])]})}),"instanceName":"1"});
            var Q25;
            Q25=makeQuery(id+"F14.opFillet","BLEND_EDGE",EDGE,{"blendedFrom":[makeQuery(id+"F8.opPattern","COPY",EDGE,{"derivedFrom":makeQuery(id+"F7.opLoft","SWEPT_EDGE",EDGE,{"disambiguationData":[OSD([sQuery(id+"F4.wireOp",EDGE,"E40.0"),sQuery(id+"F4.wireOp",EDGE,"E42"),sQuery(id+"F6.wireOp",EDGE,"E47.0"),sQuery(id+"F6.wireOp",EDGE,"E48")])]}),"instanceName":"1"}),makeQuery(id+"F8.opPattern","SPLIT",FACE,{"disambiguationData":[OD(0.0)],"derivedFrom":makeQuery(id+"F1.opRevolve","SWEPT_FACE",FACE,{"disambiguationData":[OSD([sQuery(id+"F0.wireOp",EDGE,"E21")])]})})],"blendedInto":[makeQuery(id+"F8.opPattern","SPLIT",FACE,{"disambiguationData":[OD(0.0)],"derivedFrom":makeQuery(id+"F1.opRevolve","SWEPT_FACE",FACE,{"disambiguationData":[OSD([sQuery(id+"F0.wireOp",EDGE,"E21")])]})})]});
            var Q26;
            Q26=makeQuery(id+"F8.opPattern","COPY",EDGE,{"derivedFrom":makeQuery(id+"F7.boolean.opBoolean","INTERSECT",EDGE,{"derivedFrom":[makeQuery(id+"F1.opRevolve","SWEPT_FACE",FACE,{"disambiguationData":[OSD([sQuery(id+"F0.wireOp",EDGE,"E21")])]}),makeQuery(id+"F7.opLoft","SWEPT_FACE",FACE,{"disambiguationData":[OSD([sQuery(id+"F4.wireOp",EDGE,"E40.0"),sQuery(id+"F4.wireOp",EDGE,"E40.1"),sQuery(id+"F4.wireOp",EDGE,"E40.2"),sQuery(id+"F6.wireOp",EDGE,"E47.0"),sQuery(id+"F6.wireOp",EDGE,"E47.1"),sQuery(id+"F6.wireOp",EDGE,"E47.2")])]})]}),"instanceName":"1"});
            var Q27;
            Q27=makeQuery(id+"F8.opPattern","COPY",EDGE,{"derivedFrom":makeQuery(id+"F7.boolean.opBoolean","INTERSECT",EDGE,{"derivedFrom":[makeQuery(id+"F1.opRevolve","SWEPT_FACE",FACE,{"disambiguationData":[OSD([sQuery(id+"F0.wireOp",EDGE,"E21")])]}),makeQuery(id+"F7.opLoft","SWEPT_FACE",FACE,{"disambiguationData":[OSD([sQuery(id+"F4.wireOp",EDGE,"E40.1"),sQuery(id+"F4.wireOp",EDGE,"E40.2"),sQuery(id+"F4.wireOp",EDGE,"E41"),sQuery(id+"F6.wireOp",EDGE,"E47.1"),sQuery(id+"F6.wireOp",EDGE,"E47.2"),sQuery(id+"F6.wireOp",EDGE,"E51")])]})]}),"instanceName":"1"});
            var Q28;
            Q28=makeQuery(id+"F8.opPattern","COPY",EDGE,{"derivedFrom":makeQuery(id+"F7.boolean.opBoolean","INTERSECT",EDGE,{"derivedFrom":[makeQuery(id+"F1.opRevolve","SWEPT_FACE",FACE,{"disambiguationData":[OSD([sQuery(id+"F0.wireOp",EDGE,"E20")])]}),makeQuery(id+"F7.opLoft","SWEPT_FACE",FACE,{"disambiguationData":[OSD([sQuery(id+"F4.wireOp",EDGE,"E40.1"),sQuery(id+"F4.wireOp",EDGE,"E40.2"),sQuery(id+"F4.wireOp",EDGE,"E41"),sQuery(id+"F6.wireOp",EDGE,"E47.1"),sQuery(id+"F6.wireOp",EDGE,"E47.2"),sQuery(id+"F6.wireOp",EDGE,"E51")])]})]}),"instanceName":"1"});
            var Q29;
            Q29=makeQuery(id+"F8.opPattern","COPY",EDGE,{"derivedFrom":makeQuery(id+"F7.boolean.opBoolean","INTERSECT",EDGE,{"derivedFrom":[makeQuery(id+"F1.opRevolve","SWEPT_FACE",FACE,{"disambiguationData":[OSD([sQuery(id+"F0.wireOp",EDGE,"E20")])]}),makeQuery(id+"F7.opLoft","SWEPT_FACE",FACE,{"disambiguationData":[OSD([sQuery(id+"F4.wireOp",EDGE,"E36"),sQuery(id+"F4.wireOp",EDGE,"E40.2"),sQuery(id+"F4.wireOp",EDGE,"E41"),sQuery(id+"F6.wireOp",EDGE,"E44"),sQuery(id+"F6.wireOp",EDGE,"E47.2"),sQuery(id+"F6.wireOp",EDGE,"E51")])]})]}),"instanceName":"1"});
            fillet(context, id + "F17", {"entities" : qUnion([Q0, Q1, Q2, Q3, Q4, Q5, Q6, Q7, Q8, Q9, Q10, Q11, Q12, Q13, Q14, Q15, Q16, Q17, Q18, Q19, Q20, Q21, Q22, Q23, Q24, Q25, Q26, Q27, Q28, Q29]), "radius" : 1 * mm, "tangentPropagation" : true, "allowEdgeOverflow" : false});
        }
        {
            var Q0;
            Q0=makeQuery(id+"F8.opPattern","COPY",EDGE,{"derivedFrom":makeQuery(id+"F7.boolean.opBoolean","INTERSECT",EDGE,{"derivedFrom":[makeQuery(id+"F1.opRevolve","SWEPT_FACE",FACE,{"disambiguationData":[OSD([sQuery(id+"F0.wireOp",EDGE,"E20")])]}),makeQuery(id+"F7.opLoft","SWEPT_FACE",FACE,{"disambiguationData":[OSD([sQuery(id+"F4.wireOp",EDGE,"E40.1"),sQuery(id+"F4.wireOp",EDGE,"E40.2"),sQuery(id+"F4.wireOp",EDGE,"E41"),sQuery(id+"F6.wireOp",EDGE,"E47.1"),sQuery(id+"F6.wireOp",EDGE,"E47.2"),sQuery(id+"F6.wireOp",EDGE,"E51")])]})]}),"instanceName":"2"});
            var Q1;
            Q1=makeQuery(id+"F8.opPattern","COPY",EDGE,{"derivedFrom":makeQuery(id+"F7.boolean.opBoolean","INTERSECT",EDGE,{"derivedFrom":[makeQuery(id+"F1.opRevolve","SWEPT_FACE",FACE,{"disambiguationData":[OSD([sQuery(id+"F0.wireOp",EDGE,"E20")])]}),makeQuery(id+"F7.opLoft","SWEPT_FACE",FACE,{"disambiguationData":[OSD([sQuery(id+"F4.wireOp",EDGE,"E36"),sQuery(id+"F4.wireOp",EDGE,"E40.2"),sQuery(id+"F4.wireOp",EDGE,"E41"),sQuery(id+"F6.wireOp",EDGE,"E44"),sQuery(id+"F6.wireOp",EDGE,"E47.2"),sQuery(id+"F6.wireOp",EDGE,"E51")])]})]}),"instanceName":"2"});
            var Q2;
            Q2=makeQuery(id+"F8.opPattern","COPY",EDGE,{"derivedFrom":makeQuery(id+"F7.boolean.opBoolean","INTERSECT",EDGE,{"derivedFrom":[makeQuery(id+"F1.opRevolve","SWEPT_FACE",FACE,{"disambiguationData":[OSD([sQuery(id+"F0.wireOp",EDGE,"E20")])]}),makeQuery(id+"F7.opLoft","SWEPT_FACE",FACE,{"disambiguationData":[OSD([sQuery(id+"F4.wireOp",EDGE,"E36"),sQuery(id+"F4.wireOp",EDGE,"E39.filletArc"),sQuery(id+"F4.wireOp",EDGE,"E41"),sQuery(id+"F6.wireOp",EDGE,"E44"),sQuery(id+"F6.wireOp",EDGE,"E46"),sQuery(id+"F6.wireOp",EDGE,"E51")])]})]}),"instanceName":"2"});
            var Q3;
            Q3=makeQuery(id+"F8.opPattern","COPY",EDGE,{"derivedFrom":makeQuery(id+"F7.boolean.opBoolean","INTERSECT",EDGE,{"derivedFrom":[makeQuery(id+"F1.opRevolve","SWEPT_FACE",FACE,{"disambiguationData":[OSD([sQuery(id+"F0.wireOp",EDGE,"E21")])]}),makeQuery(id+"F7.opLoft","SWEPT_FACE",FACE,{"disambiguationData":[OSD([sQuery(id+"F4.wireOp",EDGE,"E36"),sQuery(id+"F4.wireOp",EDGE,"E39.filletArc"),sQuery(id+"F4.wireOp",EDGE,"E41"),sQuery(id+"F6.wireOp",EDGE,"E44"),sQuery(id+"F6.wireOp",EDGE,"E46"),sQuery(id+"F6.wireOp",EDGE,"E51")])]})]}),"instanceName":"2"});
            var Q4;
            Q4=makeQuery(id+"F8.opPattern","COPY",EDGE,{"derivedFrom":makeQuery(id+"F7.boolean.opBoolean","INTERSECT",EDGE,{"derivedFrom":[makeQuery(id+"F1.opRevolve","SWEPT_FACE",FACE,{"disambiguationData":[OSD([sQuery(id+"F0.wireOp",EDGE,"E20")])]}),makeQuery(id+"F7.opLoft","SWEPT_FACE",FACE,{"disambiguationData":[OSD([sQuery(id+"F4.wireOp",EDGE,"E40.1"),sQuery(id+"F4.wireOp",EDGE,"E40.2"),sQuery(id+"F4.wireOp",EDGE,"E41"),sQuery(id+"F6.wireOp",EDGE,"E47.1"),sQuery(id+"F6.wireOp",EDGE,"E47.2"),sQuery(id+"F6.wireOp",EDGE,"E51")])]})]}),"instanceName":"3"});
            var Q5;
            Q5=makeQuery(id+"F8.opPattern","COPY",EDGE,{"derivedFrom":makeQuery(id+"F7.boolean.opBoolean","INTERSECT",EDGE,{"derivedFrom":[makeQuery(id+"F1.opRevolve","SWEPT_FACE",FACE,{"disambiguationData":[OSD([sQuery(id+"F0.wireOp",EDGE,"E20")])]}),makeQuery(id+"F7.opLoft","SWEPT_FACE",FACE,{"disambiguationData":[OSD([sQuery(id+"F4.wireOp",EDGE,"E36"),sQuery(id+"F4.wireOp",EDGE,"E40.2"),sQuery(id+"F4.wireOp",EDGE,"E41"),sQuery(id+"F6.wireOp",EDGE,"E44"),sQuery(id+"F6.wireOp",EDGE,"E47.2"),sQuery(id+"F6.wireOp",EDGE,"E51")])]})]}),"instanceName":"3"});
            var Q6;
            Q6=makeQuery(id+"F8.opPattern","COPY",EDGE,{"derivedFrom":makeQuery(id+"F7.boolean.opBoolean","INTERSECT",EDGE,{"derivedFrom":[makeQuery(id+"F1.opRevolve","SWEPT_FACE",FACE,{"disambiguationData":[OSD([sQuery(id+"F0.wireOp",EDGE,"E20")])]}),makeQuery(id+"F7.opLoft","SWEPT_FACE",FACE,{"disambiguationData":[OSD([sQuery(id+"F4.wireOp",EDGE,"E36"),sQuery(id+"F4.wireOp",EDGE,"E39.filletArc"),sQuery(id+"F4.wireOp",EDGE,"E41"),sQuery(id+"F6.wireOp",EDGE,"E44"),sQuery(id+"F6.wireOp",EDGE,"E46"),sQuery(id+"F6.wireOp",EDGE,"E51")])]})]}),"instanceName":"3"});
            var Q7;
            Q7=makeQuery(id+"F8.opPattern","COPY",EDGE,{"derivedFrom":makeQuery(id+"F7.boolean.opBoolean","INTERSECT",EDGE,{"derivedFrom":[makeQuery(id+"F1.opRevolve","SWEPT_FACE",FACE,{"disambiguationData":[OSD([sQuery(id+"F0.wireOp",EDGE,"E21")])]}),makeQuery(id+"F7.opLoft","SWEPT_FACE",FACE,{"disambiguationData":[OSD([sQuery(id+"F4.wireOp",EDGE,"E36"),sQuery(id+"F4.wireOp",EDGE,"E39.filletArc"),sQuery(id+"F4.wireOp",EDGE,"E41"),sQuery(id+"F6.wireOp",EDGE,"E44"),sQuery(id+"F6.wireOp",EDGE,"E46"),sQuery(id+"F6.wireOp",EDGE,"E51")])]})]}),"instanceName":"3"});
            var Q8;
            Q8=makeQuery(id+"F8.opPattern","COPY",EDGE,{"derivedFrom":makeQuery(id+"F7.boolean.opBoolean","INTERSECT",EDGE,{"derivedFrom":[makeQuery(id+"F1.opRevolve","SWEPT_FACE",FACE,{"disambiguationData":[OSD([sQuery(id+"F0.wireOp",EDGE,"E20")])]}),makeQuery(id+"F7.opLoft","SWEPT_FACE",FACE,{"disambiguationData":[OSD([sQuery(id+"F4.wireOp",EDGE,"E40.1"),sQuery(id+"F4.wireOp",EDGE,"E40.2"),sQuery(id+"F4.wireOp",EDGE,"E41"),sQuery(id+"F6.wireOp",EDGE,"E47.1"),sQuery(id+"F6.wireOp",EDGE,"E47.2"),sQuery(id+"F6.wireOp",EDGE,"E51")])]})]}),"instanceName":"4"});
            var Q9;
            Q9=makeQuery(id+"F8.opPattern","COPY",EDGE,{"derivedFrom":makeQuery(id+"F7.boolean.opBoolean","INTERSECT",EDGE,{"derivedFrom":[makeQuery(id+"F1.opRevolve","SWEPT_FACE",FACE,{"disambiguationData":[OSD([sQuery(id+"F0.wireOp",EDGE,"E20")])]}),makeQuery(id+"F7.opLoft","SWEPT_FACE",FACE,{"disambiguationData":[OSD([sQuery(id+"F4.wireOp",EDGE,"E36"),sQuery(id+"F4.wireOp",EDGE,"E40.2"),sQuery(id+"F4.wireOp",EDGE,"E41"),sQuery(id+"F6.wireOp",EDGE,"E44"),sQuery(id+"F6.wireOp",EDGE,"E47.2"),sQuery(id+"F6.wireOp",EDGE,"E51")])]})]}),"instanceName":"4"});
            var Q10;
            Q10=makeQuery(id+"F8.opPattern","COPY",EDGE,{"derivedFrom":makeQuery(id+"F7.boolean.opBoolean","INTERSECT",EDGE,{"derivedFrom":[makeQuery(id+"F1.opRevolve","SWEPT_FACE",FACE,{"disambiguationData":[OSD([sQuery(id+"F0.wireOp",EDGE,"E20")])]}),makeQuery(id+"F7.opLoft","SWEPT_FACE",FACE,{"disambiguationData":[OSD([sQuery(id+"F4.wireOp",EDGE,"E36"),sQuery(id+"F4.wireOp",EDGE,"E39.filletArc"),sQuery(id+"F4.wireOp",EDGE,"E41"),sQuery(id+"F6.wireOp",EDGE,"E44"),sQuery(id+"F6.wireOp",EDGE,"E46"),sQuery(id+"F6.wireOp",EDGE,"E51")])]})]}),"instanceName":"4"});
            var Q11;
            Q11=makeQuery(id+"F8.opPattern","COPY",EDGE,{"derivedFrom":makeQuery(id+"F7.boolean.opBoolean","INTERSECT",EDGE,{"derivedFrom":[makeQuery(id+"F1.opRevolve","SWEPT_FACE",FACE,{"disambiguationData":[OSD([sQuery(id+"F0.wireOp",EDGE,"E21")])]}),makeQuery(id+"F7.opLoft","SWEPT_FACE",FACE,{"disambiguationData":[OSD([sQuery(id+"F4.wireOp",EDGE,"E36"),sQuery(id+"F4.wireOp",EDGE,"E39.filletArc"),sQuery(id+"F4.wireOp",EDGE,"E41"),sQuery(id+"F6.wireOp",EDGE,"E44"),sQuery(id+"F6.wireOp",EDGE,"E46"),sQuery(id+"F6.wireOp",EDGE,"E51")])]})]}),"instanceName":"4"});
            fillet(context, id + "F18", {"entities" : qUnion([Q0, Q1, Q2, Q3, Q4, Q5, Q6, Q7, Q8, Q9, Q10, Q11]), "radius" : 1 * mm, "tangentPropagation" : true, "allowEdgeOverflow" : false});
        }
    });
